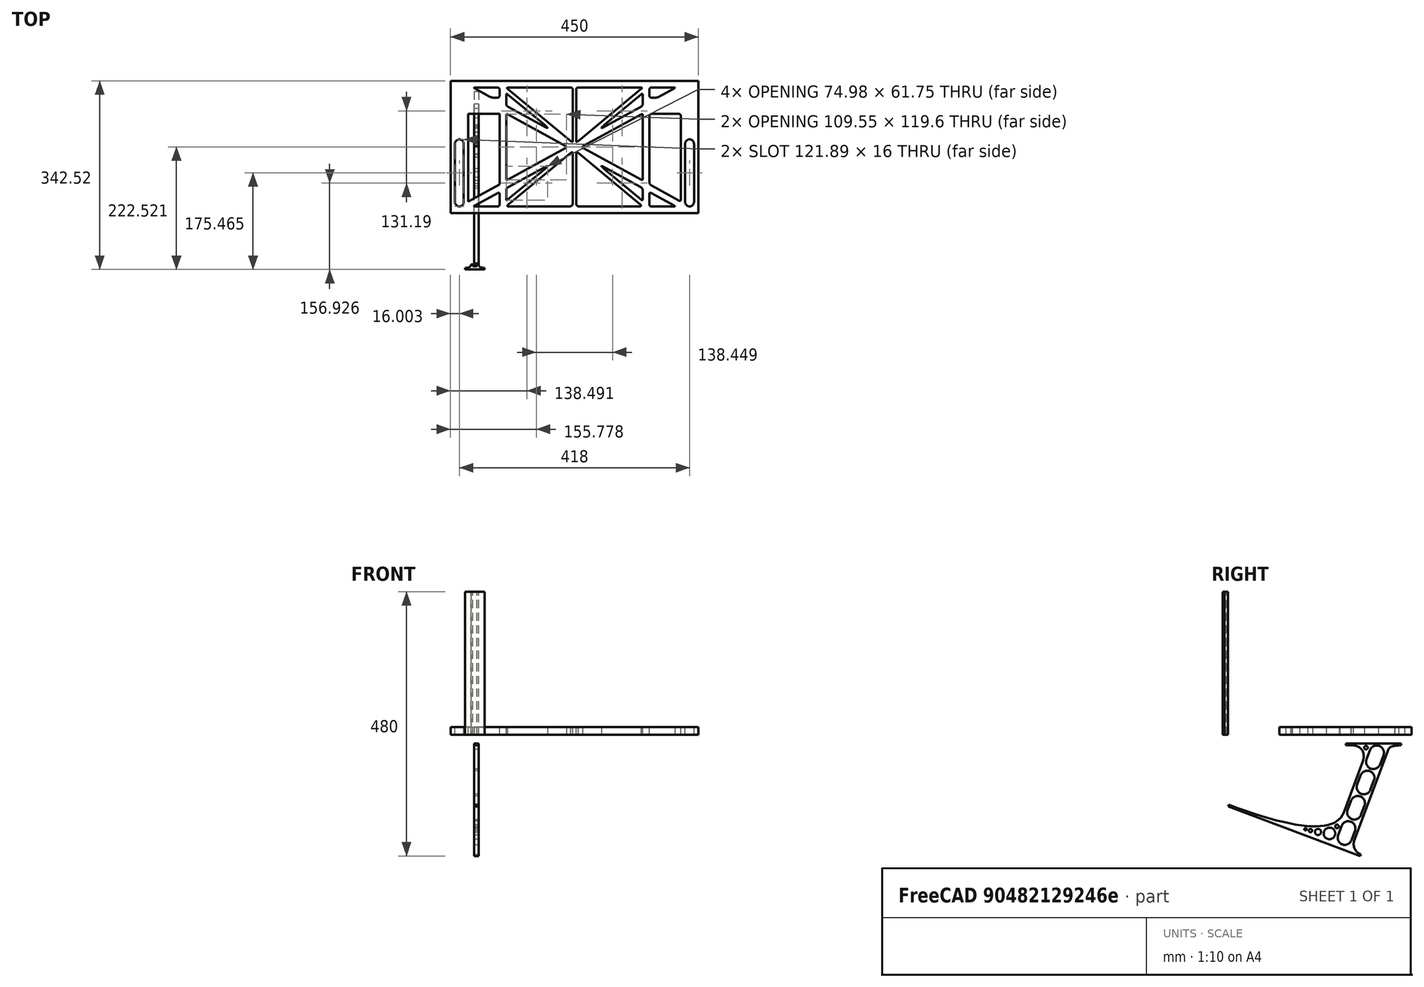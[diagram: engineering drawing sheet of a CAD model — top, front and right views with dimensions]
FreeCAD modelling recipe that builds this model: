
FCSTD DOCUMENT  (FreeCAD 0.19R0.19.2)
Label: laptopStand143FCStd
License: All rights reserved
LicenseURL: http://en.wikipedia.org/wiki/All_rights_reserved
objects: Sketcher::SketchObject×4, Part::Extrusion×3
note: 7 computed .brp shape members not serialized (recipe doc carries the construction recipe); baked Part::Feature solids carry a one-line shape summary decoded from their .brp

FEATURE [Sketcher::SketchObject] Sketch
  FullyConstrained = false
  sketch-geometry (349):
    g0: LineSegment StartX=-10.9272 StartY=-82.7794 StartZ=0 EndX=46.0728 EndY=-51.4823 EndZ=0
    g1: LineSegment StartX=-10.9272 StartY=76.4095 StartZ=0 EndX=-10.9272 EndY=-82.7794 EndZ=0
    g2: LineSegment StartX=46.0728 StartY=76.4095 StartZ=0 EndX=46.0728 EndY=-51.4823 EndZ=0
    g3: LineSegment StartX=-42.9272 StartY=136.221 StartZ=0 EndX=-42.9272 EndY=-103.779 EndZ=0
    g4: LineSegment StartX=407.073 StartY=136.221 StartZ=0 EndX=407.073 EndY=-103.779 EndZ=0
    g5: ArcOfCircle CenterX=-26.9272 CenterY=-83.7794 CenterZ=0 NormalX=0 NormalY=0 NormalZ=1 AngleXU=0 Radius=8 StartAngle=3.14159 EndAngle=6.28319
    g6: ArcOfCircle CenterX=391.073 CenterY=22.1087 CenterZ=0 NormalX=0 NormalY=0 NormalZ=1 AngleXU=0 Radius=8 StartAngle=-4.4e-15 EndAngle=3.14159
    g7: LineSegment StartX=399.073 StartY=22.1087 StartZ=0 EndX=399.073 EndY=-83.7794 EndZ=0
    g8: LineSegment StartX=383.073 StartY=22.1087 StartZ=0 EndX=383.073 EndY=-83.7794 EndZ=0
    g9: ArcOfCircle CenterX=391.073 CenterY=-83.7794 CenterZ=0 NormalX=0 NormalY=0 NormalZ=1 AngleXU=0 Radius=8 StartAngle=3.14159 EndAngle=6.28319
    g10: Circle CenterX=175.022 CenterY=27.0628 CenterZ=0 NormalX=0 NormalY=0 NormalZ=1 AngleXU=0 Radius=1
    g11: Circle CenterX=179.022 CenterY=24.8665 CenterZ=0 NormalX=0 NormalY=0 NormalZ=1 AngleXU=0 Radius=1
    g12: Circle CenterX=179.022 CenterY=27.0628 CenterZ=0 NormalX=0 NormalY=0 NormalZ=1 AngleXU=0 Radius=1
    g13: BSplineCurve PolesCount=3 KnotsCount=2 Degree=2 IsPeriodic=0
    g14: GeomPoint X=175.022 Y=27.0628 Z=0
    g15: GeomPoint X=179.022 Y=27.0628 Z=0
    g16: Circle CenterX=189.124 CenterY=27.0628 CenterZ=0 NormalX=0 NormalY=0 NormalZ=1 AngleXU=0 Radius=1
    g17: Circle CenterX=185.124 CenterY=24.8665 CenterZ=0 NormalX=0 NormalY=0 NormalZ=1 AngleXU=0 Radius=1
    g18: Circle CenterX=185.124 CenterY=27.0628 CenterZ=0 NormalX=0 NormalY=0 NormalZ=1 AngleXU=0 Radius=1
    g19: BSplineCurve PolesCount=3 KnotsCount=2 Degree=2 IsPeriodic=0
    g20: GeomPoint X=189.124 Y=27.0628 Z=0
    g21: GeomPoint X=185.124 Y=27.0628 Z=0
    g22: Circle CenterX=175.022 CenterY=5.37834 CenterZ=0 NormalX=0 NormalY=0 NormalZ=1 AngleXU=0 Radius=1
    g23: Circle CenterX=179.022 CenterY=7.57463 CenterZ=0 NormalX=0 NormalY=0 NormalZ=1 AngleXU=0 Radius=1
    g24: Circle CenterX=179.022 CenterY=5.34704 CenterZ=0 NormalX=0 NormalY=0 NormalZ=1 AngleXU=0 Radius=1
    g25: BSplineCurve PolesCount=3 KnotsCount=2 Degree=2 IsPeriodic=0
    g26: GeomPoint X=175.022 Y=5.37834 Z=0
    g27: GeomPoint X=179.022 Y=5.34704 Z=0
    g28: Circle CenterX=189.124 CenterY=5.37834 CenterZ=0 NormalX=0 NormalY=0 NormalZ=1 AngleXU=0 Radius=1
    g29: Circle CenterX=185.124 CenterY=7.57463 CenterZ=0 NormalX=0 NormalY=0 NormalZ=1 AngleXU=0 Radius=1
    g30: Circle CenterX=185.124 CenterY=5.34704 CenterZ=0 NormalX=0 NormalY=0 NormalZ=1 AngleXU=0 Radius=1
    g31: BSplineCurve PolesCount=3 KnotsCount=2 Degree=2 IsPeriodic=0
    g32: GeomPoint X=189.124 Y=5.37834 Z=0
    g33: GeomPoint X=185.124 Y=5.34704 Z=0
    g34: Circle CenterX=165.871 CenterY=18.1458 CenterZ=0 NormalX=0 NormalY=0 NormalZ=1 AngleXU=0 Radius=1
    g35: Circle CenterX=169.377 CenterY=16.2206 CenterZ=0 NormalX=0 NormalY=0 NormalZ=1 AngleXU=0 Radius=1
    g36: Circle CenterX=165.871 CenterY=14.2954 CenterZ=0 NormalX=0 NormalY=0 NormalZ=1 AngleXU=0 Radius=1
    g37: BSplineCurve PolesCount=3 KnotsCount=2 Degree=2 IsPeriodic=0
    g38: GeomPoint X=165.871 Y=18.1458 Z=0
    g39: GeomPoint X=165.871 Y=14.2954 Z=0
    g40: Circle CenterX=198.275 CenterY=18.1458 CenterZ=0 NormalX=0 NormalY=0 NormalZ=1 AngleXU=0 Radius=1
    g41: Circle CenterX=194.768 CenterY=16.2206 CenterZ=0 NormalX=0 NormalY=0 NormalZ=1 AngleXU=0 Radius=1
    g42: Circle CenterX=198.275 CenterY=14.2954 CenterZ=0 NormalX=0 NormalY=0 NormalZ=1 AngleXU=0 Radius=1
    g43: BSplineCurve PolesCount=3 KnotsCount=2 Degree=2 IsPeriodic=0
    g44: GeomPoint X=198.275 Y=18.1458 Z=0
    g45: GeomPoint X=198.275 Y=14.2954 Z=0
    g46: LineSegment StartX=407.073 StartY=-103.779 StartZ=0 EndX=-42.9272 EndY=-103.779 EndZ=0
    g47: LineSegment StartX=407.073 StartY=136.221 StartZ=0 EndX=-42.9272 EndY=136.221 EndZ=0
    g48: LineSegment StartX=46.0728 StartY=76.4095 StartZ=0 EndX=-10.9272 EndY=76.4095 EndZ=0
    g49: Circle CenterX=125.607 CenterY=54.1951 CenterZ=0 NormalX=0 NormalY=0 NormalZ=1 AngleXU=0 Radius=1
    g50: Circle CenterX=139.632 CenterY=46.4944 CenterZ=0 NormalX=0 NormalY=0 NormalZ=1 AngleXU=0 Radius=1
    g51: Circle CenterX=127.326 CenterY=56.7187 CenterZ=0 NormalX=0 NormalY=0 NormalZ=1 AngleXU=0 Radius=1
    g52: BSplineCurve PolesCount=3 KnotsCount=2 Degree=2 IsPeriodic=0
    g53: GeomPoint X=125.607 Y=54.1951 Z=0
    g54: GeomPoint X=127.326 Y=56.7187 Z=0
    g55: Circle CenterX=236.821 CenterY=56.7187 CenterZ=0 NormalX=0 NormalY=0 NormalZ=1 AngleXU=0 Radius=1
    g56: Circle CenterX=224.513 CenterY=46.4944 CenterZ=0 NormalX=0 NormalY=0 NormalZ=1 AngleXU=0 Radius=1
    g57: Circle CenterX=238.538 CenterY=54.1951 CenterZ=0 NormalX=0 NormalY=0 NormalZ=1 AngleXU=0 Radius=1
    g58: BSplineCurve PolesCount=3 KnotsCount=2 Degree=2 IsPeriodic=0
    g59: GeomPoint X=236.821 Y=56.7187 Z=0
    g60: GeomPoint X=238.538 Y=54.1951 Z=0
    g61: Circle CenterX=238.538 CenterY=-21.7539 CenterZ=0 NormalX=0 NormalY=0 NormalZ=1 AngleXU=0 Radius=1
    g62: Circle CenterX=224.513 CenterY=-14.0532 CenterZ=0 NormalX=0 NormalY=0 NormalZ=1 AngleXU=0 Radius=1
    g63: Circle CenterX=236.821 CenterY=-24.2775 CenterZ=0 NormalX=0 NormalY=0 NormalZ=1 AngleXU=0 Radius=1
    g64: BSplineCurve PolesCount=3 KnotsCount=2 Degree=2 IsPeriodic=0
    g65: GeomPoint X=238.538 Y=-21.7539 Z=0
    g66: GeomPoint X=236.821 Y=-24.2775 Z=0
    g67: Circle CenterX=125.607 CenterY=-21.7539 CenterZ=0 NormalX=0 NormalY=0 NormalZ=1 AngleXU=0 Radius=1
    g68: Circle CenterX=139.632 CenterY=-14.0532 CenterZ=0 NormalX=0 NormalY=0 NormalZ=1 AngleXU=0 Radius=1
    g69: Circle CenterX=127.325 CenterY=-24.2775 CenterZ=0 NormalX=0 NormalY=0 NormalZ=1 AngleXU=0 Radius=1
    g70: BSplineCurve PolesCount=3 KnotsCount=2 Degree=2 IsPeriodic=0
    g71: GeomPoint X=125.607 Y=-21.7539 Z=0
    g72: GeomPoint X=127.325 Y=-24.2775 Z=0
    g73: Circle CenterX=302.996 CenterY=111.695 CenterZ=0 NormalX=0 NormalY=0 NormalZ=1 AngleXU=0 Radius=1
    g74: Circle CenterX=306.073 CenterY=114.251 CenterZ=0 NormalX=0 NormalY=0 NormalZ=1 AngleXU=0 Radius=1
    g75: Circle CenterX=306.073 CenterY=110.251 CenterZ=0 NormalX=0 NormalY=0 NormalZ=1 AngleXU=0 Radius=1
    g76: BSplineCurve PolesCount=3 KnotsCount=2 Degree=2 IsPeriodic=0
    g77: GeomPoint X=302.996 Y=111.695 Z=0
    g78: GeomPoint X=306.073 Y=110.251 Z=0
    g79: Circle CenterX=306.073 CenterY=95.2763 CenterZ=0 NormalX=0 NormalY=0 NormalZ=1 AngleXU=0 Radius=1
    g80: Circle CenterX=306.073 CenterY=91.2763 CenterZ=0 NormalX=0 NormalY=0 NormalZ=1 AngleXU=0 Radius=1
    g81: Circle CenterX=302.567 CenterY=89.3511 CenterZ=0 NormalX=0 NormalY=0 NormalZ=1 AngleXU=0 Radius=1
    g82: BSplineCurve PolesCount=3 KnotsCount=2 Degree=2 IsPeriodic=0
    g83: GeomPoint X=306.073 Y=95.2763 Z=0
    g84: GeomPoint X=302.567 Y=89.3511 Z=0
    g85: LineSegment StartX=306.073 StartY=110.251 StartZ=0 EndX=306.073 EndY=95.2763 EndZ=0
    g86: LineSegment StartX=302.996 StartY=111.695 StartZ=0 EndX=236.821 EndY=56.7187 EndZ=0
    g87: LineSegment StartX=238.538 StartY=54.1951 StartZ=0 EndX=302.567 EndY=89.3511 EndZ=0
    g88: Circle CenterX=61.1496 CenterY=111.695 CenterZ=0 NormalX=0 NormalY=0 NormalZ=1 AngleXU=0 Radius=1
    g89: Circle CenterX=58.0728 CenterY=114.251 CenterZ=0 NormalX=0 NormalY=0 NormalZ=1 AngleXU=0 Radius=1
    g90: Circle CenterX=58.0728 CenterY=110.251 CenterZ=0 NormalX=0 NormalY=0 NormalZ=1 AngleXU=0 Radius=1
    g91: BSplineCurve PolesCount=3 KnotsCount=2 Degree=2 IsPeriodic=0
    g92: GeomPoint X=61.1496 Y=111.695 Z=0
    g93: GeomPoint X=58.0728 Y=110.251 Z=0
    g94: Circle CenterX=61.5791 CenterY=89.3511 CenterZ=0 NormalX=0 NormalY=0 NormalZ=1 AngleXU=0 Radius=1
    g95: Circle CenterX=58.0728 CenterY=91.2763 CenterZ=0 NormalX=0 NormalY=0 NormalZ=1 AngleXU=0 Radius=1
    g96: Circle CenterX=58.0728 CenterY=95.2763 CenterZ=0 NormalX=0 NormalY=0 NormalZ=1 AngleXU=0 Radius=1
    g97: BSplineCurve PolesCount=3 KnotsCount=2 Degree=2 IsPeriodic=0
    g98: GeomPoint X=61.5791 Y=89.3511 Z=0
    g99: GeomPoint X=58.0728 Y=95.2763 Z=0
    g100: LineSegment StartX=58.0728 StartY=110.251 StartZ=0 EndX=58.0728 EndY=95.2763 EndZ=0
    g101: LineSegment StartX=61.1496 StartY=111.695 StartZ=0 EndX=127.326 EndY=56.7187 EndZ=0
    g102: LineSegment StartX=125.607 StartY=54.1951 StartZ=0 EndX=61.5791 EndY=89.3511 EndZ=0
    g103: Circle CenterX=61.5791 CenterY=-56.9099 CenterZ=0 NormalX=0 NormalY=0 NormalZ=1 AngleXU=0 Radius=1
    g104: Circle CenterX=58.0728 CenterY=-58.8351 CenterZ=0 NormalX=0 NormalY=0 NormalZ=1 AngleXU=0 Radius=1
    g105: Circle CenterX=58.0728 CenterY=-62.8351 CenterZ=0 NormalX=0 NormalY=0 NormalZ=1 AngleXU=0 Radius=1
    g106: BSplineCurve PolesCount=3 KnotsCount=2 Degree=2 IsPeriodic=0
    g107: GeomPoint X=61.5791 Y=-56.9099 Z=0
    g108: GeomPoint X=58.0728 Y=-62.8351 Z=0
    g109: Circle CenterX=58.0728 CenterY=-77.8102 CenterZ=0 NormalX=0 NormalY=0 NormalZ=1 AngleXU=0 Radius=1
    g110: Circle CenterX=58.0728 CenterY=-81.8102 CenterZ=0 NormalX=0 NormalY=0 NormalZ=1 AngleXU=0 Radius=1
    g111: Circle CenterX=61.1496 CenterY=-79.2541 CenterZ=0 NormalX=0 NormalY=0 NormalZ=1 AngleXU=0 Radius=1
    g112: BSplineCurve PolesCount=3 KnotsCount=2 Degree=2 IsPeriodic=0
    g113: GeomPoint X=58.0728 Y=-77.8102 Z=0
    g114: GeomPoint X=61.1496 Y=-79.2541 Z=0
    g115: LineSegment StartX=58.0728 StartY=-62.8351 StartZ=0 EndX=58.0728 EndY=-77.8102 EndZ=0
    g116: LineSegment StartX=61.1496 StartY=-79.2541 StartZ=0 EndX=127.325 EndY=-24.2775 EndZ=0
    g117: LineSegment StartX=125.607 StartY=-21.7539 StartZ=0 EndX=61.5791 EndY=-56.9099 EndZ=0
    g118: Circle CenterX=302.567 CenterY=-56.9099 CenterZ=0 NormalX=0 NormalY=0 NormalZ=1 AngleXU=0 Radius=1
    g119: Circle CenterX=306.073 CenterY=-58.8351 CenterZ=0 NormalX=0 NormalY=0 NormalZ=1 AngleXU=0 Radius=1
    g120: Circle CenterX=306.073 CenterY=-62.8351 CenterZ=0 NormalX=0 NormalY=0 NormalZ=1 AngleXU=0 Radius=1
    g121: BSplineCurve PolesCount=3 KnotsCount=2 Degree=2 IsPeriodic=0
    g122: GeomPoint X=302.567 Y=-56.9099 Z=0
    g123: GeomPoint X=306.073 Y=-62.8351 Z=0
    g124: Circle CenterX=302.996 CenterY=-79.2541 CenterZ=0 NormalX=0 NormalY=0 NormalZ=1 AngleXU=0 Radius=1
    g125: Circle CenterX=306.073 CenterY=-81.8102 CenterZ=0 NormalX=0 NormalY=0 NormalZ=1 AngleXU=0 Radius=1
    g126: Circle CenterX=306.073 CenterY=-77.8102 CenterZ=0 NormalX=0 NormalY=0 NormalZ=1 AngleXU=0 Radius=1
    g127: BSplineCurve PolesCount=3 KnotsCount=2 Degree=2 IsPeriodic=0
    g128: GeomPoint X=302.996 Y=-79.2541 Z=0
    g129: GeomPoint X=306.073 Y=-77.8102 Z=0
    g130: LineSegment StartX=306.073 StartY=-62.8351 StartZ=0 EndX=306.073 EndY=-77.8102 EndZ=0
    g131: LineSegment StartX=302.996 StartY=-79.2541 StartZ=0 EndX=236.821 EndY=-24.2775 EndZ=0
    g132: LineSegment StartX=238.538 StartY=-21.7539 StartZ=0 EndX=302.567 EndY=-56.9099 EndZ=0
    g133: Circle CenterX=61.6457 CenterY=-88.8112 CenterZ=0 NormalX=0 NormalY=0 NormalZ=1 AngleXU=0 Radius=1
    g134: Circle CenterX=58.0728 CenterY=-91.7794 CenterZ=0 NormalX=0 NormalY=0 NormalZ=1 AngleXU=0 Radius=1
    g135: Circle CenterX=63.9135 CenterY=-91.7794 CenterZ=0 NormalX=0 NormalY=0 NormalZ=1 AngleXU=0 Radius=1
    g136: BSplineCurve PolesCount=3 KnotsCount=2 Degree=2 IsPeriodic=0
    g137: GeomPoint X=61.6457 Y=-88.8112 Z=0
    g138: GeomPoint X=63.9135 Y=-91.7794 Z=0
    g139: Circle CenterX=179.022 CenterY=-85.8163 CenterZ=0 NormalX=0 NormalY=0 NormalZ=1 AngleXU=0 Radius=1
    g140: Circle CenterX=179.022 CenterY=-91.7794 CenterZ=0 NormalX=0 NormalY=0 NormalZ=1 AngleXU=0 Radius=1
    g141: Circle CenterX=171.895 CenterY=-91.7794 CenterZ=0 NormalX=0 NormalY=0 NormalZ=1 AngleXU=0 Radius=1
    g142: BSplineCurve PolesCount=3 KnotsCount=2 Degree=2 IsPeriodic=0
    g143: GeomPoint X=179.022 Y=-85.8163 Z=0
    g144: GeomPoint X=171.895 Y=-91.7794 Z=0
    g145: Circle CenterX=185.124 CenterY=-86.2028 CenterZ=0 NormalX=0 NormalY=0 NormalZ=1 AngleXU=0 Radius=1
    g146: Circle CenterX=185.124 CenterY=-91.7794 CenterZ=0 NormalX=0 NormalY=0 NormalZ=1 AngleXU=0 Radius=1
    g147: Circle CenterX=191.747 CenterY=-91.7794 CenterZ=0 NormalX=0 NormalY=0 NormalZ=1 AngleXU=0 Radius=1
    g148: BSplineCurve PolesCount=3 KnotsCount=2 Degree=2 IsPeriodic=0
    g149: GeomPoint X=185.124 Y=-86.2028 Z=0
    g150: GeomPoint X=191.747 Y=-91.7794 Z=0
    g151: Circle CenterX=299.888 CenterY=-86.6413 CenterZ=0 NormalX=0 NormalY=0 NormalZ=1 AngleXU=0 Radius=1
    g152: Circle CenterX=306.073 CenterY=-91.7794 CenterZ=0 NormalX=0 NormalY=0 NormalZ=1 AngleXU=0 Radius=1
    g153: Circle CenterX=298.776 CenterY=-91.7794 CenterZ=0 NormalX=0 NormalY=0 NormalZ=1 AngleXU=0 Radius=1
    g154: BSplineCurve PolesCount=3 KnotsCount=2 Degree=2 IsPeriodic=0
    g155: GeomPoint X=299.888 Y=-86.6413 Z=0
    g156: GeomPoint X=298.776 Y=-91.7794 Z=0
    g157: LineSegment StartX=189.124 StartY=5.37834 StartZ=0 EndX=299.888 EndY=-86.6413 EndZ=0
    g158: LineSegment StartX=298.776 StartY=-91.7794 StartZ=0 EndX=191.747 EndY=-91.7794 EndZ=0
    g159: LineSegment StartX=185.124 StartY=-86.2028 StartZ=0 EndX=185.124 EndY=5.34704 EndZ=0
    g160: LineSegment StartX=179.022 StartY=5.34704 StartZ=0 EndX=179.022 EndY=-85.8163 EndZ=0
    g161: LineSegment StartX=171.895 StartY=-91.7794 StartZ=0 EndX=63.9135 EndY=-91.7794 EndZ=0
    g162: LineSegment StartX=61.6457 StartY=-88.8112 StartZ=0 EndX=175.022 EndY=5.37834 EndZ=0
    g163: Circle CenterX=302.073 CenterY=124.221 CenterZ=0 NormalX=0 NormalY=0 NormalZ=1 AngleXU=0 Radius=1
    g164: Circle CenterX=306.073 CenterY=124.221 CenterZ=0 NormalX=0 NormalY=0 NormalZ=1 AngleXU=0 Radius=1
    g165: Circle CenterX=302.996 CenterY=121.665 CenterZ=0 NormalX=0 NormalY=0 NormalZ=1 AngleXU=0 Radius=1
    g166: BSplineCurve PolesCount=3 KnotsCount=2 Degree=2 IsPeriodic=0
    g167: GeomPoint X=302.073 Y=124.221 Z=0
    g168: GeomPoint X=302.996 Y=121.665 Z=0
    g169: Circle CenterX=189.124 CenterY=124.221 CenterZ=0 NormalX=0 NormalY=0 NormalZ=1 AngleXU=0 Radius=1
    g170: Circle CenterX=185.124 CenterY=124.221 CenterZ=0 NormalX=0 NormalY=0 NormalZ=1 AngleXU=0 Radius=1
    g171: Circle CenterX=185.124 CenterY=120.221 CenterZ=0 NormalX=0 NormalY=0 NormalZ=1 AngleXU=0 Radius=1
    g172: BSplineCurve PolesCount=3 KnotsCount=2 Degree=2 IsPeriodic=0
    g173: GeomPoint X=189.124 Y=124.221 Z=0
    g174: GeomPoint X=185.124 Y=120.221 Z=0
    g175: Circle CenterX=175.022 CenterY=124.221 CenterZ=0 NormalX=0 NormalY=0 NormalZ=1 AngleXU=0 Radius=1
    g176: Circle CenterX=179.022 CenterY=124.221 CenterZ=0 NormalX=0 NormalY=0 NormalZ=1 AngleXU=0 Radius=1
    g177: Circle CenterX=179.022 CenterY=120.221 CenterZ=0 NormalX=0 NormalY=0 NormalZ=1 AngleXU=0 Radius=1
    g178: BSplineCurve PolesCount=3 KnotsCount=2 Degree=2 IsPeriodic=0
    g179: GeomPoint X=175.022 Y=124.221 Z=0
    g180: GeomPoint X=179.022 Y=120.221 Z=0
    g181: Circle CenterX=62.0728 CenterY=124.221 CenterZ=0 NormalX=0 NormalY=0 NormalZ=1 AngleXU=0 Radius=1
    g182: Circle CenterX=58.0728 CenterY=124.221 CenterZ=0 NormalX=0 NormalY=0 NormalZ=1 AngleXU=0 Radius=1
    g183: Circle CenterX=61.1496 CenterY=121.665 CenterZ=0 NormalX=0 NormalY=0 NormalZ=1 AngleXU=0 Radius=1
    g184: BSplineCurve PolesCount=3 KnotsCount=2 Degree=2 IsPeriodic=0
    g185: GeomPoint X=62.0728 Y=124.221 Z=0
    g186: GeomPoint X=61.1496 Y=121.665 Z=0
    g187: LineSegment StartX=62.0728 StartY=124.221 StartZ=0 EndX=175.022 EndY=124.221 EndZ=0
    g188: LineSegment StartX=179.022 StartY=120.221 StartZ=0 EndX=179.022 EndY=27.0628 EndZ=0
    g189: LineSegment StartX=185.124 StartY=27.0628 StartZ=0 EndX=185.124 EndY=120.221 EndZ=0
    g190: LineSegment StartX=189.124 StartY=124.221 StartZ=0 EndX=302.073 EndY=124.221 EndZ=0
    g191: LineSegment StartX=302.996 StartY=121.665 StartZ=0 EndX=189.124 EndY=27.0628 EndZ=0
    g192: LineSegment StartX=175.022 StartY=27.0628 StartZ=0 EndX=61.1496 EndY=121.665 EndZ=0
    g193: Circle CenterX=61.5791 CenterY=75.4095 CenterZ=0 NormalX=0 NormalY=0 NormalZ=1 AngleXU=0 Radius=1
    g194: Circle CenterX=58.0728 CenterY=77.3346 CenterZ=0 NormalX=0 NormalY=0 NormalZ=1 AngleXU=0 Radius=1
    g195: Circle CenterX=58.0728 CenterY=73.3346 CenterZ=0 NormalX=0 NormalY=0 NormalZ=1 AngleXU=0 Radius=1
    g196: BSplineCurve PolesCount=3 KnotsCount=2 Degree=2 IsPeriodic=0
    g197: GeomPoint X=61.5791 Y=75.4095 Z=0
    g198: GeomPoint X=58.0728 Y=73.3346 Z=0
    g199: Circle CenterX=58.0728 CenterY=-40.8935 CenterZ=0 NormalX=0 NormalY=0 NormalZ=1 AngleXU=0 Radius=1
    g200: Circle CenterX=58.0728 CenterY=-44.8935 CenterZ=0 NormalX=0 NormalY=0 NormalZ=1 AngleXU=0 Radius=1
    g201: Circle CenterX=61.5791 CenterY=-42.9683 CenterZ=0 NormalX=0 NormalY=0 NormalZ=1 AngleXU=0 Radius=1
    g202: BSplineCurve PolesCount=3 KnotsCount=2 Degree=2 IsPeriodic=0
    g203: GeomPoint X=58.0728 Y=-40.8935 Z=0
    g204: GeomPoint X=61.5791 Y=-42.9683 Z=0
    g205: LineSegment StartX=61.5791 StartY=-42.9683 StartZ=0 EndX=165.871 EndY=14.2954 EndZ=0
    g206: LineSegment StartX=165.871 StartY=18.1458 StartZ=0 EndX=61.5791 EndY=75.4095 EndZ=0
    g207: LineSegment StartX=58.0728 StartY=73.3346 StartZ=0 EndX=58.0728 EndY=-40.8935 EndZ=0
    g208: Circle CenterX=302.567 CenterY=-42.9683 CenterZ=0 NormalX=0 NormalY=0 NormalZ=1 AngleXU=0 Radius=1
    g209: Circle CenterX=306.073 CenterY=-44.8935 CenterZ=0 NormalX=0 NormalY=0 NormalZ=1 AngleXU=0 Radius=1
    g210: Circle CenterX=306.073 CenterY=-40.8935 CenterZ=0 NormalX=0 NormalY=0 NormalZ=1 AngleXU=0 Radius=1
    g211: BSplineCurve PolesCount=3 KnotsCount=2 Degree=2 IsPeriodic=0
    g212: GeomPoint X=302.567 Y=-42.9683 Z=0
    g213: GeomPoint X=306.073 Y=-40.8935 Z=0
    g214: Circle CenterX=306.073 CenterY=73.3346 CenterZ=0 NormalX=0 NormalY=0 NormalZ=1 AngleXU=0 Radius=1
    g215: Circle CenterX=306.073 CenterY=77.3346 CenterZ=0 NormalX=0 NormalY=0 NormalZ=1 AngleXU=0 Radius=1
    g216: Circle CenterX=302.567 CenterY=75.4095 CenterZ=0 NormalX=0 NormalY=0 NormalZ=1 AngleXU=0 Radius=1
    g217: BSplineCurve PolesCount=3 KnotsCount=2 Degree=2 IsPeriodic=0
    g218: GeomPoint X=306.073 Y=73.3346 Z=0
    g219: GeomPoint X=302.567 Y=75.4095 Z=0
    g220: LineSegment StartX=302.567 StartY=-42.9683 StartZ=0 EndX=198.275 EndY=14.2954 EndZ=0
    g221: LineSegment StartX=198.275 StartY=18.1458 StartZ=0 EndX=302.567 EndY=75.4095 EndZ=0
    g222: LineSegment StartX=306.073 StartY=73.3346 StartZ=0 EndX=306.073 EndY=-40.8935 EndZ=0
    g223: LineSegment StartX=322.073 StartY=105.865 StartZ=0 EndX=328.643 EndY=105.865 EndZ=0
    g224: LineSegment StartX=318.073 StartY=120.221 StartZ=0 EndX=318.073 EndY=109.865 EndZ=0
    g225: LineSegment StartX=336.157 StartY=107.779 StartZ=0 EndX=362.567 EndY=122.294 EndZ=0
    g226: Circle CenterX=362.073 CenterY=124.221 CenterZ=0 NormalX=0 NormalY=0 NormalZ=1 AngleXU=0 Radius=1
    g227: Circle CenterX=366.073 CenterY=124.221 CenterZ=0 NormalX=0 NormalY=0 NormalZ=1 AngleXU=0 Radius=1
    g228: Circle CenterX=362.567 CenterY=122.294 CenterZ=0 NormalX=0 NormalY=0 NormalZ=1 AngleXU=0 Radius=1
    g229: BSplineCurve PolesCount=3 KnotsCount=2 Degree=2 IsPeriodic=0
    g230: GeomPoint X=362.073 Y=124.221 Z=0
    g231: GeomPoint X=362.567 Y=122.294 Z=0
    g232: Circle CenterX=322.073 CenterY=124.221 CenterZ=0 NormalX=0 NormalY=0 NormalZ=1 AngleXU=0 Radius=1
    g233: Circle CenterX=318.073 CenterY=124.221 CenterZ=0 NormalX=0 NormalY=0 NormalZ=1 AngleXU=0 Radius=1
    g234: Circle CenterX=318.073 CenterY=120.221 CenterZ=0 NormalX=0 NormalY=0 NormalZ=1 AngleXU=0 Radius=1
    g235: BSplineCurve PolesCount=3 KnotsCount=2 Degree=2 IsPeriodic=0
    g236: GeomPoint X=322.073 Y=124.221 Z=0
    g237: GeomPoint X=318.073 Y=120.221 Z=0
    g238: Circle CenterX=322.073 CenterY=105.865 CenterZ=0 NormalX=0 NormalY=0 NormalZ=1 AngleXU=0 Radius=1
    g239: Circle CenterX=318.073 CenterY=105.865 CenterZ=0 NormalX=0 NormalY=0 NormalZ=1 AngleXU=0 Radius=1
    g240: Circle CenterX=318.073 CenterY=109.865 CenterZ=0 NormalX=0 NormalY=0 NormalZ=1 AngleXU=0 Radius=1
    g241: BSplineCurve PolesCount=3 KnotsCount=2 Degree=2 IsPeriodic=0
    g242: GeomPoint X=322.073 Y=105.865 Z=0
    g243: GeomPoint X=318.073 Y=109.865 Z=0
    g244: Circle CenterX=336.157 CenterY=107.779 CenterZ=0 NormalX=0 NormalY=0 NormalZ=1 AngleXU=0 Radius=1
    g245: Circle CenterX=332.651 CenterY=105.853 CenterZ=0 NormalX=0 NormalY=0 NormalZ=1 AngleXU=0 Radius=1
    g246: Circle CenterX=328.643 CenterY=105.865 CenterZ=0 NormalX=0 NormalY=0 NormalZ=1 AngleXU=0 Radius=1
    g247: BSplineCurve PolesCount=3 KnotsCount=2 Degree=2 IsPeriodic=0
    g248: GeomPoint X=336.157 Y=107.779 Z=0
    g249: GeomPoint X=328.643 Y=105.865 Z=0
    g250: LineSegment StartX=322.073 StartY=124.221 StartZ=0 EndX=362.073 EndY=124.221 EndZ=0
    g251: Circle CenterX=371.567 CenterY=-80.8644 CenterZ=0 NormalX=0 NormalY=0 NormalZ=1 AngleXU=0 Radius=1
    g252: Circle CenterX=375.073 CenterY=-82.7896 CenterZ=0 NormalX=0 NormalY=0 NormalZ=1 AngleXU=0 Radius=1
    g253: Circle CenterX=375.073 CenterY=-78.7896 CenterZ=0 NormalX=0 NormalY=0 NormalZ=1 AngleXU=0 Radius=1
    g254: BSplineCurve PolesCount=3 KnotsCount=2 Degree=2 IsPeriodic=0
    g255: GeomPoint X=371.567 Y=-80.8644 Z=0
    g256: GeomPoint X=375.073 Y=-78.7896 Z=0
    g257: Circle CenterX=321.579 CenterY=-53.4075 CenterZ=0 NormalX=0 NormalY=0 NormalZ=1 AngleXU=0 Radius=1
    g258: Circle CenterX=318.073 CenterY=-51.4823 CenterZ=0 NormalX=0 NormalY=0 NormalZ=1 AngleXU=0 Radius=1
    g259: Circle CenterX=318.073 CenterY=-47.4805 CenterZ=0 NormalX=0 NormalY=0 NormalZ=1 AngleXU=0 Radius=1
    g260: BSplineCurve PolesCount=3 KnotsCount=2 Degree=2 IsPeriodic=0
    g261: GeomPoint X=321.579 Y=-53.4075 Z=0
    g262: GeomPoint X=318.073 Y=-47.4805 Z=0
    g263: LineSegment StartX=371.567 StartY=-80.8644 StartZ=0 EndX=321.579 EndY=-53.4075 EndZ=0
    g264: Circle CenterX=321.579 CenterY=-67.3492 CenterZ=0 NormalX=0 NormalY=0 NormalZ=1 AngleXU=0 Radius=1
    g265: Circle CenterX=318.073 CenterY=-65.424 CenterZ=0 NormalX=0 NormalY=0 NormalZ=1 AngleXU=0 Radius=1
    g266: Circle CenterX=318.073 CenterY=-69.424 CenterZ=0 NormalX=0 NormalY=0 NormalZ=1 AngleXU=0 Radius=1
    g267: BSplineCurve PolesCount=3 KnotsCount=2 Degree=2 IsPeriodic=0
    g268: GeomPoint X=321.579 Y=-67.3492 Z=0
    g269: GeomPoint X=318.073 Y=-69.424 Z=0
    g270: Circle CenterX=362.567 CenterY=-89.8542 CenterZ=0 NormalX=0 NormalY=0 NormalZ=1 AngleXU=0 Radius=1
    g271: Circle CenterX=366.073 CenterY=-91.7794 CenterZ=0 NormalX=0 NormalY=0 NormalZ=1 AngleXU=0 Radius=1
    g272: Circle CenterX=362.073 CenterY=-91.7794 CenterZ=0 NormalX=0 NormalY=0 NormalZ=1 AngleXU=0 Radius=1
    g273: BSplineCurve PolesCount=3 KnotsCount=2 Degree=2 IsPeriodic=0
    g274: GeomPoint X=362.567 Y=-89.8542 Z=0
    g275: GeomPoint X=362.073 Y=-91.7794 Z=0
    g276: Circle CenterX=322.073 CenterY=-91.7794 CenterZ=0 NormalX=0 NormalY=0 NormalZ=1 AngleXU=0 Radius=1
    g277: Circle CenterX=318.073 CenterY=-91.7794 CenterZ=0 NormalX=0 NormalY=0 NormalZ=1 AngleXU=0 Radius=1
    g278: Circle CenterX=318.073 CenterY=-87.7794 CenterZ=0 NormalX=0 NormalY=0 NormalZ=1 AngleXU=0 Radius=1
    g279: BSplineCurve PolesCount=3 KnotsCount=2 Degree=2 IsPeriodic=0
    g280: GeomPoint X=322.073 Y=-91.7794 Z=0
    g281: GeomPoint X=318.073 Y=-87.7794 Z=0
    g282: LineSegment StartX=362.567 StartY=-89.8542 StartZ=0 EndX=321.579 EndY=-67.3492 EndZ=0
    g283: LineSegment StartX=318.073 StartY=-69.424 StartZ=0 EndX=318.073 EndY=-87.7794 EndZ=0
    g284: LineSegment StartX=322.073 StartY=-91.7794 StartZ=0 EndX=362.073 EndY=-91.7794 EndZ=0
    g285: Circle CenterX=2.07281 CenterY=124.221 CenterZ=0 NormalX=0 NormalY=0 NormalZ=1 AngleXU=0 Radius=1
    g286: Circle CenterX=1.57905 CenterY=122.295 CenterZ=0 NormalX=0 NormalY=0 NormalZ=1 AngleXU=0 Radius=1
    g287: BSplineCurve PolesCount=3 KnotsCount=2 Degree=2 IsPeriodic=0
    g288: GeomPoint X=2.07281 Y=124.221 Z=0
    g289: GeomPoint X=1.57905 Y=122.295 Z=0
    g290: Circle CenterX=42.0728 CenterY=124.221 CenterZ=0 NormalX=0 NormalY=0 NormalZ=1 AngleXU=0 Radius=1
    g291: Circle CenterX=46.0728 CenterY=124.221 CenterZ=0 NormalX=0 NormalY=0 NormalZ=1 AngleXU=0 Radius=1
    g292: Circle CenterX=46.0728 CenterY=120.221 CenterZ=0 NormalX=0 NormalY=0 NormalZ=1 AngleXU=0 Radius=1
    g293: BSplineCurve PolesCount=3 KnotsCount=2 Degree=2 IsPeriodic=0
    g294: GeomPoint X=42.0728 Y=124.221 Z=0
    g295: GeomPoint X=46.0728 Y=120.221 Z=0
    g296: Circle CenterX=46.0728 CenterY=109.865 CenterZ=0 NormalX=0 NormalY=0 NormalZ=1 AngleXU=0 Radius=1
    g297: Circle CenterX=46.0728 CenterY=105.865 CenterZ=0 NormalX=0 NormalY=0 NormalZ=1 AngleXU=0 Radius=1
    g298: Circle CenterX=42.0728 CenterY=105.865 CenterZ=0 NormalX=0 NormalY=0 NormalZ=1 AngleXU=0 Radius=1
    g299: BSplineCurve PolesCount=3 KnotsCount=2 Degree=2 IsPeriodic=0
    g300: GeomPoint X=46.0728 Y=109.865 Z=0
    g301: GeomPoint X=42.0728 Y=105.865 Z=0
    g302: Circle CenterX=35.5028 CenterY=105.865 CenterZ=0 NormalX=0 NormalY=0 NormalZ=1 AngleXU=0 Radius=1
    g303: Circle CenterX=31.5028 CenterY=105.865 CenterZ=0 NormalX=0 NormalY=0 NormalZ=1 AngleXU=0 Radius=1
    g304: Circle CenterX=27.9965 CenterY=107.79 CenterZ=0 NormalX=0 NormalY=0 NormalZ=1 AngleXU=0 Radius=1
    g305: BSplineCurve PolesCount=3 KnotsCount=2 Degree=2 IsPeriodic=0
    g306: GeomPoint X=35.5028 Y=105.865 Z=0
    g307: GeomPoint X=27.9965 Y=107.79 Z=0
    g308: LineSegment StartX=2.07281 StartY=124.221 StartZ=0 EndX=42.0728 EndY=124.221 EndZ=0
    g309: LineSegment StartX=46.0728 StartY=120.221 StartZ=0 EndX=46.0728 EndY=109.865 EndZ=0
    g310: LineSegment StartX=42.0728 StartY=105.865 StartZ=0 EndX=35.5028 EndY=105.865 EndZ=0
    g311: LineSegment StartX=27.9965 StartY=107.79 StartZ=0 EndX=1.57905 EndY=122.295 EndZ=0
    g312: Circle CenterX=42.5666 CenterY=-67.3492 CenterZ=0 NormalX=0 NormalY=0 NormalZ=1 AngleXU=0 Radius=1
    g313: Circle CenterX=46.0728 CenterY=-65.424 CenterZ=0 NormalX=0 NormalY=0 NormalZ=1 AngleXU=0 Radius=1
    g314: Circle CenterX=46.0728 CenterY=-69.424 CenterZ=0 NormalX=0 NormalY=0 NormalZ=1 AngleXU=0 Radius=1
    g315: BSplineCurve PolesCount=3 KnotsCount=2 Degree=2 IsPeriodic=0
    g316: GeomPoint X=42.5666 Y=-67.3492 Z=0
    g317: GeomPoint X=46.0728 Y=-69.424 Z=0
    g318: Circle CenterX=46.0728 CenterY=-87.7794 CenterZ=0 NormalX=0 NormalY=0 NormalZ=1 AngleXU=0 Radius=1
    g319: Circle CenterX=46.0728 CenterY=-91.7794 CenterZ=0 NormalX=0 NormalY=0 NormalZ=1 AngleXU=0 Radius=1
    g320: Circle CenterX=42.0728 CenterY=-91.7794 CenterZ=0 NormalX=0 NormalY=0 NormalZ=1 AngleXU=0 Radius=1
    g321: BSplineCurve PolesCount=3 KnotsCount=2 Degree=2 IsPeriodic=0
    g322: GeomPoint X=46.0728 Y=-87.7794 Z=0
    g323: GeomPoint X=42.0728 Y=-91.7794 Z=0
    g324: Circle CenterX=2.07281 CenterY=-91.7794 CenterZ=0 NormalX=0 NormalY=0 NormalZ=1 AngleXU=0 Radius=1
    g325: Circle CenterX=-1.92719 CenterY=-91.7794 CenterZ=0 NormalX=0 NormalY=0 NormalZ=1 AngleXU=0 Radius=1
    g326: Circle CenterX=1.57905 CenterY=-89.8542 CenterZ=0 NormalX=0 NormalY=0 NormalZ=1 AngleXU=0 Radius=1
    g327: BSplineCurve PolesCount=3 KnotsCount=2 Degree=2 IsPeriodic=0
    g328: GeomPoint X=2.07281 Y=-91.7794 Z=0
    g329: GeomPoint X=1.57905 Y=-89.8542 Z=0
    g330: LineSegment StartX=2.07281 StartY=-91.7794 StartZ=0 EndX=42.0728 EndY=-91.7794 EndZ=0
    g331: LineSegment StartX=46.0728 StartY=-87.7794 StartZ=0 EndX=46.0728 EndY=-69.424 EndZ=0
    g332: LineSegment StartX=42.5666 StartY=-67.3492 StartZ=0 EndX=1.57905 EndY=-89.8542 EndZ=0
    g333: Circle CenterX=322.073 CenterY=76.4095 CenterZ=0 NormalX=0 NormalY=0 NormalZ=1 AngleXU=0 Radius=4
    g334: BSplineCurve PolesCount=3 KnotsCount=2 Degree=2 IsPeriodic=0
    g335: GeomPoint X=318.073 Y=72.4095 Z=0
    g336: GeomPoint X=322.073 Y=76.4095 Z=0
    g337: Circle CenterX=375.073 CenterY=72.4095 CenterZ=0 NormalX=0 NormalY=0 NormalZ=1 AngleXU=0 Radius=1
    g338: Circle CenterX=375.073 CenterY=76.4095 CenterZ=0 NormalX=0 NormalY=0 NormalZ=1 AngleXU=0 Radius=1
    g339: Circle CenterX=371.073 CenterY=76.4095 CenterZ=0 NormalX=0 NormalY=0 NormalZ=1 AngleXU=0 Radius=1
    g340: BSplineCurve PolesCount=3 KnotsCount=2 Degree=2 IsPeriodic=0
    g341: GeomPoint X=375.073 Y=72.4095 Z=0
    g342: GeomPoint X=371.073 Y=76.4095 Z=0
    g343: LineSegment StartX=322.073 StartY=76.4095 StartZ=0 EndX=371.073 EndY=76.4095 EndZ=0
    g344: LineSegment StartX=318.073 StartY=72.4095 StartZ=0 EndX=318.073 EndY=-47.4805 EndZ=0
    g345: LineSegment StartX=375.073 StartY=72.4095 StartZ=0 EndX=375.073 EndY=-78.7896 EndZ=0
    g346: ArcOfCircle CenterX=-26.9272 CenterY=22.1087 CenterZ=0 NormalX=0 NormalY=0 NormalZ=1 AngleXU=0 Radius=4 StartAngle=5e-16 EndAngle=3.14159
    g347: LineSegment StartX=-30.9272 StartY=22.1087 StartZ=0 EndX=-34.9272 EndY=-83.7794 EndZ=0
    g348: LineSegment StartX=-18.9272 StartY=-83.7794 StartZ=0 EndX=-22.9272 EndY=22.1087 EndZ=0
  constraints (572):
    c: Coincident(g0,g2)
    c: Block(g0)
    c: Block(g1)
    c: Vertical(g3)
    c: Vertical(g4)
    c: Block(g4)
    c: Block(g3)
    c: Tangent(g6,g7) = 1.5708
    c: Tangent(g7,g9) = 1.5708
    c: Equal(g6,g9)
    c: Coincident(g8,g6)
    c: Coincident(g8,g9)
    c: Block(g7)
    c: Block(g8)
    c: Weight(g10) = 1
    c: Equal(g10,g11)
    c: Equal(g10,g12)
    c: InternalAlignment(g10,g13)
    c: InternalAlignment(g11,g13)
    c: InternalAlignment(g12,g13)
    c: InternalAlignment(g14,g13)
    c: InternalAlignment(g15,g13)
    c: Weight(g16) = 1
    c: Equal(g16,g17)
    c: Equal(g16,g18)
    c: InternalAlignment(g16,g19)
    c: InternalAlignment(g17,g19)
    c: InternalAlignment(g18,g19)
    c: InternalAlignment(g20,g19)
    c: InternalAlignment(g21,g19)
    c: Block(g19)
    c: Block(g13)
    c: Weight(g22) = 1
    c: Equal(g22,g23)
    c: Equal(g22,g24)
    c: InternalAlignment(g22,g25)
    c: InternalAlignment(g23,g25)
    c: InternalAlignment(g24,g25)
    c: InternalAlignment(g26,g25)
    c: InternalAlignment(g27,g25)
    c: Weight(g28) = 1
    c: Equal(g28,g29)
    c: Equal(g28,g30)
    c: InternalAlignment(g28,g31)
    c: InternalAlignment(g29,g31)
    c: InternalAlignment(g30,g31)
    c: InternalAlignment(g32,g31)
    c: InternalAlignment(g33,g31)
    c: Block(g31)
    c: Block(g25)
    c: Weight(g34) = 1
    c: Equal(g34,g35)
    c: Equal(g34,g36)
    c: InternalAlignment(g34,g37)
    c: InternalAlignment(g35,g37)
    c: InternalAlignment(g36,g37)
    c: InternalAlignment(g38,g37)
    c: InternalAlignment(g39,g37)
    c: Weight(g40) = 1
    c: Equal(g40,g41)
    c: Equal(g40,g42)
    c: InternalAlignment(g40,g43)
    c: InternalAlignment(g41,g43)
    c: InternalAlignment(g42,g43)
    c: InternalAlignment(g44,g43)
    c: InternalAlignment(g45,g43)
    c: Block(g37)
    c: Block(g43)
    c: Coincident(g46,g4)
    c: Coincident(g46,g3)
    c: Horizontal(g46)
    c: Distance(g46) = 450
    c: Coincident(g47,g4)
    c: Coincident(g47,g3)
    c: Horizontal(g47)
    c: Horizontal(g48)
    c: Coincident(g2,g48)
    c: Block(g48)
    c: Coincident(g1,g48)
    c: Weight(g49) = 1
    c: Equal(g49,g50)
    c: Equal(g49,g51)
    c: InternalAlignment(g49,g52)
    c: InternalAlignment(g50,g52)
    c: InternalAlignment(g51,g52)
    c: InternalAlignment(g53,g52)
    c: InternalAlignment(g54,g52)
    c: Block(g52)
    c: Weight(g55) = 1
    c: Equal(g55,g56)
    c: Equal(g55,g57)
    c: InternalAlignment(g55,g58)
    c: InternalAlignment(g56,g58)
    c: InternalAlignment(g57,g58)
    c: InternalAlignment(g59,g58)
    c: InternalAlignment(g60,g58)
    c: Block(g58)
    c: Weight(g61) = 1
    c: Equal(g61,g62)
    c: Equal(g61,g63)
    c: InternalAlignment(g61,g64)
    c: InternalAlignment(g62,g64)
    c: InternalAlignment(g63,g64)
    c: InternalAlignment(g65,g64)
    c: InternalAlignment(g66,g64)
    c: Block(g64)
    c: Weight(g67) = 1
    c: Equal(g67,g68)
    c: Equal(g67,g69)
    c: InternalAlignment(g67,g70)
    c: InternalAlignment(g68,g70)
    c: InternalAlignment(g69,g70)
    c: InternalAlignment(g71,g70)
    c: InternalAlignment(g72,g70)
    c: Block(g70)
    c: Weight(g73) = 1
    c: Equal(g73,g74)
    c: Equal(g73,g75)
    c: InternalAlignment(g73,g76)
    c: InternalAlignment(g74,g76)
    c: InternalAlignment(g75,g76)
    c: InternalAlignment(g77,g76)
    c: InternalAlignment(g78,g76)
    c: Weight(g79) = 1
    c: Equal(g79,g80)
    c: Equal(g79,g81)
    c: InternalAlignment(g79,g82)
    c: InternalAlignment(g80,g82)
    c: InternalAlignment(g81,g82)
    c: InternalAlignment(g83,g82)
    c: InternalAlignment(g84,g82)
    c: Block(g76)
    c: Block(g82)
    c: Coincident(g85,g76)
    c: Coincident(g85,g82)
    c: Vertical(g85)
    c: Coincident(g86,g76)
    c: Coincident(g86,g58)
    c: Coincident(g87,g58)
    c: Coincident(g87,g82)
    c: Weight(g88) = 1
    c: Equal(g88,g89)
    c: Equal(g88,g90)
    c: InternalAlignment(g88,g91)
    c: InternalAlignment(g89,g91)
    c: InternalAlignment(g90,g91)
    c: InternalAlignment(g92,g91)
    c: InternalAlignment(g93,g91)
    c: Weight(g94) = 1
    c: Equal(g94,g95)
    c: Equal(g94,g96)
    c: InternalAlignment(g94,g97)
    c: InternalAlignment(g95,g97)
    c: InternalAlignment(g96,g97)
    c: InternalAlignment(g98,g97)
    c: InternalAlignment(g99,g97)
    c: Block(g91)
    c: Block(g97)
    c: Coincident(g100,g91)
    c: Coincident(g100,g97)
    c: Vertical(g100)
    c: Coincident(g101,g91)
    c: Coincident(g101,g52)
    c: Coincident(g102,g52)
    c: Coincident(g102,g97)
    c: Weight(g103) = 1
    c: Equal(g103,g104)
    c: Equal(g103,g105)
    c: InternalAlignment(g103,g106)
    c: InternalAlignment(g104,g106)
    c: InternalAlignment(g105,g106)
    c: InternalAlignment(g107,g106)
    c: InternalAlignment(g108,g106)
    c: Weight(g109) = 1
    c: Equal(g109,g110)
    c: Equal(g109,g111)
    c: InternalAlignment(g109,g112)
    c: InternalAlignment(g110,g112)
    c: InternalAlignment(g111,g112)
    c: InternalAlignment(g113,g112)
    c: InternalAlignment(g114,g112)
    c: Block(g106)
    c: Block(g112)
    c: Coincident(g115,g106)
    c: Coincident(g115,g112)
    c: Vertical(g115)
    c: Coincident(g116,g112)
    c: Coincident(g116,g70)
    c: Coincident(g117,g70)
    c: Coincident(g117,g106)
    c: Weight(g118) = 1
    c: Equal(g118,g119)
    c: Equal(g118,g120)
    c: InternalAlignment(g118,g121)
    c: InternalAlignment(g119,g121)
    c: InternalAlignment(g120,g121)
    c: InternalAlignment(g122,g121)
    c: InternalAlignment(g123,g121)
    c: Weight(g124) = 1
    c: Equal(g124,g125)
    c: Equal(g124,g126)
    c: InternalAlignment(g124,g127)
    c: InternalAlignment(g125,g127)
    c: InternalAlignment(g126,g127)
    c: InternalAlignment(g128,g127)
    c: InternalAlignment(g129,g127)
    c: Block(g121)
    c: Block(g127)
    c: Coincident(g130,g121)
    c: Coincident(g130,g127)
    c: Vertical(g130)
    c: Coincident(g131,g127)
    c: Coincident(g131,g64)
    c: Coincident(g132,g64)
    c: Coincident(g132,g121)
    c: Weight(g133) = 1
    c: Equal(g133,g134)
    c: Equal(g133,g135)
    c: InternalAlignment(g133,g136)
    c: InternalAlignment(g134,g136)
    c: InternalAlignment(g135,g136)
    c: InternalAlignment(g137,g136)
    c: InternalAlignment(g138,g136)
    c: Weight(g139) = 1
    c: Equal(g139,g140)
    c: Equal(g139,g141)
    c: InternalAlignment(g139,g142)
    c: InternalAlignment(g140,g142)
    c: InternalAlignment(g141,g142)
    c: InternalAlignment(g143,g142)
    c: InternalAlignment(g144,g142)
    c: Weight(g145) = 1
    c: Equal(g145,g146)
    c: Equal(g145,g147)
    c: InternalAlignment(g145,g148)
    c: InternalAlignment(g146,g148)
    c: InternalAlignment(g147,g148)
    c: InternalAlignment(g149,g148)
    c: InternalAlignment(g150,g148)
    c: Weight(g151) = 1
    c: Equal(g151,g152)
    c: Equal(g151,g153)
    c: InternalAlignment(g151,g154)
    c: InternalAlignment(g152,g154)
    c: InternalAlignment(g153,g154)
    c: InternalAlignment(g155,g154)
    c: InternalAlignment(g156,g154)
    c: Block(g154)
    c: Block(g148)
    c: Block(g142)
    c: Block(g136)
    c: Coincident(g157,g31)
    c: Coincident(g157,g154)
    c: Coincident(g158,g154)
    c: Coincident(g158,g148)
    c: Horizontal(g158)
    c: Coincident(g159,g148)
    c: Coincident(g159,g31)
    c: Vertical(g159)
    c: Coincident(g160,g25)
    c: Coincident(g160,g142)
    c: Vertical(g160)
    c: Coincident(g161,g142)
    c: Coincident(g161,g136)
    c: Horizontal(g161)
    c: Coincident(g162,g136)
    c: Coincident(g162,g25)
    c: Weight(g163) = 1
    c: Equal(g163,g164)
    c: Equal(g163,g165)
    c: InternalAlignment(g163,g166)
    c: InternalAlignment(g164,g166)
    c: InternalAlignment(g165,g166)
    c: InternalAlignment(g167,g166)
    c: InternalAlignment(g168,g166)
    c: Weight(g169) = 1
    c: Equal(g169,g170)
    c: Equal(g169,g171)
    c: InternalAlignment(g169,g172)
    c: InternalAlignment(g170,g172)
    c: InternalAlignment(g171,g172)
    c: InternalAlignment(g173,g172)
    c: InternalAlignment(g174,g172)
    c: Weight(g175) = 1
    c: Equal(g175,g176)
    c: Equal(g175,g177)
    c: InternalAlignment(g175,g178)
    c: InternalAlignment(g176,g178)
    c: InternalAlignment(g177,g178)
    c: InternalAlignment(g179,g178)
    c: InternalAlignment(g180,g178)
    c: Weight(g181) = 1
    c: Equal(g181,g182)
    c: Equal(g181,g183)
    c: InternalAlignment(g181,g184)
    c: InternalAlignment(g182,g184)
    c: InternalAlignment(g183,g184)
    c: InternalAlignment(g185,g184)
    c: InternalAlignment(g186,g184)
    c: Block(g184)
    c: Block(g178)
    c: Block(g172)
    c: Block(g166)
    c: Coincident(g187,g184)
    c: Coincident(g187,g178)
    c: Horizontal(g187)
    c: Coincident(g188,g178)
    c: Coincident(g188,g13)
    c: Vertical(g188)
    c: Coincident(g189,g19)
    c: Coincident(g189,g172)
    c: Vertical(g189)
    c: Coincident(g190,g172)
    c: Coincident(g190,g166)
    c: Horizontal(g190)
    c: Coincident(g191,g166)
    c: Coincident(g191,g19)
    c: Coincident(g192,g13)
    c: Weight(g193) = 1
    c: Equal(g193,g194)
    c: Equal(g193,g195)
    c: InternalAlignment(g193,g196)
    c: InternalAlignment(g194,g196)
    c: InternalAlignment(g195,g196)
    c: InternalAlignment(g197,g196)
    c: InternalAlignment(g198,g196)
    c: Weight(g199) = 1
    c: Equal(g199,g200)
    c: Equal(g199,g201)
    c: InternalAlignment(g199,g202)
    c: InternalAlignment(g200,g202)
    c: InternalAlignment(g201,g202)
    c: InternalAlignment(g203,g202)
    c: InternalAlignment(g204,g202)
    c: Block(g202)
    c: Block(g196)
    c: Coincident(g205,g202)
    c: Coincident(g205,g37)
    c: Coincident(g206,g37)
    c: Coincident(g206,g196)
    c: Coincident(g207,g196)
    c: Coincident(g207,g202)
    c: Vertical(g207)
    c: Weight(g208) = 1
    c: Equal(g208,g209)
    c: Equal(g208,g210)
    c: InternalAlignment(g208,g211)
    c: InternalAlignment(g209,g211)
    c: InternalAlignment(g210,g211)
    c: InternalAlignment(g212,g211)
    c: InternalAlignment(g213,g211)
    c: Weight(g214) = 1
    c: Equal(g214,g215)
    c: Equal(g214,g216)
    c: InternalAlignment(g214,g217)
    c: InternalAlignment(g215,g217)
    c: InternalAlignment(g216,g217)
    c: InternalAlignment(g218,g217)
    c: InternalAlignment(g219,g217)
    c: Block(g217)
    c: Block(g211)
    c: Coincident(g220,g211)
    c: Coincident(g220,g43)
    c: Coincident(g221,g43)
    c: Coincident(g221,g217)
    c: Coincident(g222,g217)
    c: Coincident(g222,g211)
    c: Vertical(g222)
    c: Horizontal(g223)
    c: Block(g223)
    c: Vertical(g224)
    c: Block(g224)
    c: Block(g225)
    c: Weight(g226) = 1
    c: Equal(g226,g227)
    c: Equal(g226,g228)
    c: InternalAlignment(g226,g229)
    c: InternalAlignment(g227,g229)
    c: InternalAlignment(g228,g229)
    c: InternalAlignment(g230,g229)
    c: InternalAlignment(g231,g229)
    c: Weight(g232) = 1
    c: Equal(g232,g233)
    c: Equal(g232,g234)
    c: InternalAlignment(g232,g235)
    c: InternalAlignment(g233,g235)
    c: InternalAlignment(g234,g235)
    c: InternalAlignment(g236,g235)
    c: InternalAlignment(g237,g235)
    c: Weight(g238) = 1
    c: Equal(g238,g239)
    c: Equal(g238,g240)
    c: InternalAlignment(g238,g241)
    c: InternalAlignment(g239,g241)
    c: InternalAlignment(g240,g241)
    c: InternalAlignment(g242,g241)
    c: InternalAlignment(g243,g241)
    c: Weight(g244) = 1
    c: Equal(g244,g245)
    c: Equal(g244,g246)
    c: InternalAlignment(g244,g247)
    c: InternalAlignment(g245,g247)
    c: InternalAlignment(g246,g247)
    c: InternalAlignment(g248,g247)
    c: InternalAlignment(g249,g247)
    c: Block(g229)
    c: Block(g235)
    c: Block(g241)
    c: Block(g247)
    c: Coincident(g250,g235)
    c: Coincident(g250,g229)
    c: Horizontal(g250)
    c: Block(g192)
    c: Weight(g251) = 1
    c: Equal(g251,g252)
    c: Equal(g251,g253)
    c: InternalAlignment(g251,g254)
    c: InternalAlignment(g252,g254)
    c: InternalAlignment(g253,g254)
    c: InternalAlignment(g255,g254)
    c: InternalAlignment(g256,g254)
    c: Weight(g257) = 1
    c: Equal(g257,g258)
    c: Equal(g257,g259)
    c: InternalAlignment(g257,g260)
    c: InternalAlignment(g258,g260)
    c: InternalAlignment(g259,g260)
    c: InternalAlignment(g261,g260)
    c: InternalAlignment(g262,g260)
    c: Block(g254)
    c: Block(g260)
    c: Coincident(g263,g254)
    c: Coincident(g263,g260)
    c: Weight(g264) = 1
    c: Equal(g264,g265)
    c: Equal(g264,g266)
    c: InternalAlignment(g264,g267)
    c: InternalAlignment(g265,g267)
    c: InternalAlignment(g266,g267)
    c: InternalAlignment(g268,g267)
    c: InternalAlignment(g269,g267)
    c: Weight(g270) = 1
    c: Equal(g270,g271)
    c: Equal(g270,g272)
    c: InternalAlignment(g270,g273)
    c: InternalAlignment(g271,g273)
    c: InternalAlignment(g272,g273)
    c: InternalAlignment(g274,g273)
    c: InternalAlignment(g275,g273)
    c: Weight(g276) = 1
    c: Equal(g276,g277)
    c: Equal(g276,g278)
    c: InternalAlignment(g276,g279)
    c: InternalAlignment(g277,g279)
    c: InternalAlignment(g278,g279)
    c: InternalAlignment(g280,g279)
    c: InternalAlignment(g281,g279)
    c: Block(g279)
    c: Block(g273)
    c: Block(g267)
    c: Coincident(g282,g273)
    c: Coincident(g282,g267)
    c: Coincident(g283,g267)
    c: Coincident(g283,g279)
    c: Vertical(g283)
    c: Coincident(g284,g279)
    c: Coincident(g284,g273)
    c: Horizontal(g284)
    c: Weight(g285) = 1
    c: Equal(g285,g286)
    c: InternalAlignment(g285,g287)
    c: InternalAlignment(g286,g287)
    c: InternalAlignment(g288,g287)
    c: InternalAlignment(g289,g287)
    c: Weight(g290) = 1
    c: InternalAlignment(g291,g293)
    c: InternalAlignment(g292,g293)
    c: InternalAlignment(g294,g293)
    c: InternalAlignment(g295,g293)
    c: Weight(g296) = 1
    c: Equal(g296,g297)
    c: Equal(g296,g298)
    c: InternalAlignment(g296,g299)
    c: InternalAlignment(g297,g299)
    c: InternalAlignment(g298,g299)
    c: InternalAlignment(g300,g299)
    c: InternalAlignment(g301,g299)
    c: Equal(g302,g303)
    c: Equal(g302,g304)
    c: InternalAlignment(g302,g305)
    c: InternalAlignment(g303,g305)
    c: InternalAlignment(g304,g305)
    c: InternalAlignment(g306,g305)
    c: InternalAlignment(g307,g305)
    c: Block(g293)
    c: Block(g299)
    c: Block(g305)
    c: Block(g287)
    c: Coincident(g308,g287)
    c: Coincident(g308,g293)
    c: Horizontal(g308)
    c: Coincident(g309,g293)
    c: Coincident(g309,g299)
    c: Vertical(g309)
    c: Coincident(g310,g299)
    c: Coincident(g310,g305)
    c: Horizontal(g310)
    c: Coincident(g311,g305)
    c: Coincident(g311,g287)
    c: Weight(g312) = 1
    c: Equal(g312,g313)
    c: Equal(g312,g314)
    c: InternalAlignment(g312,g315)
    c: InternalAlignment(g313,g315)
    c: InternalAlignment(g314,g315)
    c: InternalAlignment(g316,g315)
    c: InternalAlignment(g317,g315)
    c: Weight(g318) = 1
    c: Equal(g318,g319)
    c: Equal(g318,g320)
    c: InternalAlignment(g318,g321)
    c: InternalAlignment(g319,g321)
    c: InternalAlignment(g320,g321)
    c: InternalAlignment(g322,g321)
    c: InternalAlignment(g323,g321)
    c: Weight(g324) = 1
    c: Equal(g324,g325)
    c: Equal(g324,g326)
    c: InternalAlignment(g324,g327)
    c: InternalAlignment(g325,g327)
    c: InternalAlignment(g326,g327)
    c: InternalAlignment(g328,g327)
    c: InternalAlignment(g329,g327)
    c: Block(g327)
    c: Block(g321)
    c: Block(g315)
    c: Coincident(g330,g327)
    c: Coincident(g330,g321)
    c: Horizontal(g330)
    c: Coincident(g331,g321)
    c: Coincident(g331,g315)
    c: Vertical(g331)
    c: Coincident(g332,g315)
    c: Coincident(g332,g327)
    c: InternalAlignment(g333,g334)
    c: InternalAlignment(g335,g334)
    c: InternalAlignment(g336,g334)
    c: Block(g334)
    c: Equal(g337,g338)
    c: Equal(g337,g339)
    c: InternalAlignment(g337,g340)
    c: InternalAlignment(g338,g340)
    c: InternalAlignment(g339,g340)
    c: InternalAlignment(g341,g340)
    c: InternalAlignment(g342,g340)
    c: Block(g340)
    c: Coincident(g343,g334)
    c: Horizontal(g343)
    c: Block(g343)
    c: Coincident(g344,g334)
    c: Coincident(g344,g260)
    c: Vertical(g344)
    c: Coincident(g345,g340)
    c: Coincident(g345,g254)
    c: Vertical(g345)
    c: Coincident(g347,g5)
    c: Coincident(g348,g5)
    c: Block(g346)
    c: Block(g5)
    c: Block(g348)
    c: Block(g347)
    c: Distance(g344) = 119.89
FEATURE [Sketcher::SketchObject] Sketch001
  FullyConstrained = true
  MapMode = 4
  Placement = pos=(0,0,0) rot=(0.57735,0.57735,0.57735;2.0944rad)
  Support = -> [Sketch]
  sketch-geometry (46):
    g0: BSplineCurve PolesCount=3 KnotsCount=2 Degree=2 IsPeriodic=0
    g1: ArcOfCircle CenterX=73.1223 CenterY=-32.291 CenterZ=0 NormalX=0 NormalY=0 NormalZ=1 AngleXU=0 Radius=13 StartAngle=5.92268 EndAngle=9.06428
    g2: ArcOfCircle CenterX=66.7816 CenterY=-49.1439 CenterZ=0 NormalX=0 NormalY=0 NormalZ=1 AngleXU=0 Radius=13 StartAngle=2.78068 EndAngle=5.92131
    g3: ArcOfCircle CenterX=55.9263 CenterY=-78.1807 CenterZ=0 NormalX=0 NormalY=0 NormalZ=1 AngleXU=0 Radius=13 StartAngle=5.92268 EndAngle=9.06428
    g4: ArcOfCircle CenterX=49.5884 CenterY=-95.0342 CenterZ=0 NormalX=0 NormalY=0 NormalZ=1 AngleXU=0 Radius=13 StartAngle=2.78068 EndAngle=5.92131
    g5: ArcOfCircle CenterX=38.7206 CenterY=-124.067 CenterZ=0 NormalX=0 NormalY=0 NormalZ=1 AngleXU=0 Radius=13 StartAngle=5.92268 EndAngle=9.06428
    g6: ArcOfCircle CenterX=32.3875 CenterY=-140.92 CenterZ=0 NormalX=0 NormalY=0 NormalZ=1 AngleXU=0 Radius=13 StartAngle=2.78068 EndAngle=5.92131
    g7: ArcOfCircle CenterX=21.4715 CenterY=-169.934 CenterZ=0 NormalX=0 NormalY=0 NormalZ=1 AngleXU=0 Radius=13 StartAngle=5.92268 EndAngle=9.06428
    g8: ArcOfCircle CenterX=15.1336 CenterY=-186.787 CenterZ=0 NormalX=0 NormalY=0 NormalZ=1 AngleXU=0 Radius=13 StartAngle=2.78068 EndAngle=5.92131
    g9-g12: Circle x4 (B-spline internal-alignment scaffolding for g13; pole/knot coordinates omitted)
    g13: BSplineCurve PolesCount=4 KnotsCount=2 Degree=3 IsPeriodic=0
    g14: GeomPoint X=28.8094 Y=-19.0875 Z=0
    g15: GeomPoint X=47.0443 Y=-50.4712 Z=0
    g16: Circle CenterX=53.5586 CenterY=-23.2695 CenterZ=0 NormalX=0 NormalY=0 NormalZ=1 AngleXU=0 Radius=3.24518
    g17: Circle CenterX=-195.441 CenterY=-127.082 CenterZ=0 NormalX=0 NormalY=0 NormalZ=1 AngleXU=0 Radius=1
    g18: Circle CenterX=-8.24091 CenterY=-197.481 CenterZ=0 NormalX=0 NormalY=0 NormalZ=1 AngleXU=0 Radius=1
    g19: Circle CenterX=12.8789 CenterY=-141.321 CenterZ=0 NormalX=0 NormalY=0 NormalZ=1 AngleXU=0 Radius=1
    g20: BSplineCurve PolesCount=3 KnotsCount=2 Degree=2 IsPeriodic=0
    g21: GeomPoint X=-195.441 Y=-127.082 Z=0
    g22: GeomPoint X=12.8789 Y=-141.321 Z=0
    g23: Circle CenterX=-12.8016 CenterY=-179.036 CenterZ=0 NormalX=0 NormalY=0 NormalZ=1 AngleXU=0 Radius=10.5072
    g24: Circle CenterX=0.933922 CenterY=-166.43 CenterZ=0 NormalX=0 NormalY=0 NormalZ=1 AngleXU=0 Radius=3.26661
    g25: Circle CenterX=-33.5518 CenterY=-176.44 CenterZ=0 NormalX=0 NormalY=0 NormalZ=1 AngleXU=0 Radius=5.64388
    g26: Circle CenterX=-47.2366 CenterY=-173.859 CenterZ=0 NormalX=0 NormalY=0 NormalZ=1 AngleXU=0 Radius=3.01653
    g27: Circle CenterX=-56.2595 CenterY=-171.456 CenterZ=0 NormalX=0 NormalY=0 NormalZ=1 AngleXU=0 Radius=2.12826
    g28: ArcOfCircle CenterX=51.2151 CenterY=-198.473 CenterZ=0 NormalX=0 NormalY=0 NormalZ=1 AngleXU=0 Radius=20 StartAngle=2.78189 EndAngle=4.35269
    g29: LineSegment StartX=32.4951 StartY=-191.433 StartZ=0 EndX=94.6578 EndY=-26.1352 EndZ=0
    g30: LineSegment StartX=43.1192 StartY=-220.001 StartZ=0 EndX=-196.497 EndY=-129.89 EndZ=0
    g31: LineSegment StartX=43.1192 StartY=-220.001 StartZ=0 EndX=44.1752 EndY=-217.193 EndZ=0
    g32: LineSegment StartX=117.223 StartY=-19.0875 StartZ=0 EndX=117.223 EndY=-16.0875 EndZ=0
    g33: LineSegment StartX=117.223 StartY=-16.0875 StartZ=0 EndX=17.2232 EndY=-16.0875 EndZ=0
    g34: LineSegment StartX=17.2232 StartY=-16.0875 StartZ=0 EndX=17.2232 EndY=-19.0875 EndZ=0
    g35: LineSegment StartX=28.8094 StartY=-19.0875 StartZ=0 EndX=17.2232 EndY=-19.0875 EndZ=0
    g36: LineSegment StartX=47.0443 StartY=-50.4712 StartZ=0 EndX=12.8789 EndY=-141.321 EndZ=0
    g37: LineSegment StartX=-195.441 StartY=-127.082 StartZ=0 EndX=-196.497 EndY=-129.89 EndZ=0
    g38: LineSegment StartX=85.2866 StartY=-36.8766 StartZ=0 EndX=78.9396 EndY=-53.7463 EndZ=0
    g39: LineSegment StartX=60.9579 StartY=-27.7053 StartZ=0 EndX=54.6191 EndY=-44.5532 EndZ=0
    g40: LineSegment StartX=68.0907 StartY=-82.7664 StartZ=0 EndX=61.7465 EndY=-99.6365 EndZ=0
    g41: LineSegment StartX=43.7619 StartY=-73.595 StartZ=0 EndX=37.426 EndY=-90.4435 EndZ=0
    g42: LineSegment StartX=50.885 StartY=-128.652 StartZ=0 EndX=44.5456 EndY=-145.522 EndZ=0
    g43: LineSegment StartX=26.5562 StartY=-119.481 StartZ=0 EndX=20.2251 EndY=-136.329 EndZ=0
    g44: LineSegment StartX=9.3071 StartY=-165.349 StartZ=0 EndX=2.97115 EndY=-182.197 EndZ=0
    g45: LineSegment StartX=33.6358 StartY=-174.52 StartZ=0 EndX=27.2917 EndY=-191.39 EndZ=0
  constraints (71):
    c: Block(g0)
    c: Block(g1)
    c: Block(g2)
    c: Block(g4)
    c: Block(g3)
    c: Block(g6)
    c: Block(g5)
    c: Block(g8)
    c: Block(g7)
    c: Weight(g9) = 1
    c: Equal(g9,g10)
    c: Equal(g9,g11)
    c: Equal(g9,g12)
    c: InternalAlignment(g9-g12 -> g13) x4
    c: InternalAlignment(g14,g13)
    c: InternalAlignment(g15,g13)
    c: Block(g16)
    c: Weight(g17) = 1
    c: Equal(g17,g18)
    c: Equal(g17,g19)
    c: InternalAlignment(g17,g20)
    c: InternalAlignment(g18,g20)
    c: InternalAlignment(g19,g20)
    c: InternalAlignment(g21,g20)
    c: InternalAlignment(g22,g20)
    c: Block(g20)
    c: Block(g23)
    c: Block(g24)
    c: Block(g25)
    c: Block(g26)
    c: Block(g27)
    c: Block(g28)
    c: Coincident(g29,g28)
    c: Coincident(g29,g0)
    c: Block(g13)
    c: Coincident(g31,g30)
    c: Coincident(g31,g28)
    c: Block(g31)
    c: Coincident(g32,g0)
    c: Vertical(g32)
    c: Coincident(g33,g32)
    c: Horizontal(g33)
    c: Coincident(g34,g33)
    c: Vertical(g34)
    c: Block(g33)
    c: Coincident(g35,g13)
    c: Coincident(g35,g34)
    c: Horizontal(g35)
    c: Coincident(g36,g13)
    c: Coincident(g36,g20)
    c: Coincident(g37,g20)
    c: Coincident(g37,g30)
    c: Block(g30)
    c: Coincident(g38,g1)
    c: Coincident(g38,g2)
    c: Coincident(g39,g1)
    c: Coincident(g39,g2)
    c: Coincident(g40,g3)
    c: Coincident(g40,g4)
    c: Coincident(g41,g3)
    c: Coincident(g41,g4)
    c: Coincident(g42,g5)
    c: Coincident(g42,g6)
    c: Coincident(g43,g5)
    c: Coincident(g43,g6)
    c: Coincident(g44,g7)
    c: Coincident(g44,g8)
    c: Coincident(g45,g7)
    c: Coincident(g45,g8)
    c: Distance(g30) = 256
    c: Distance(g33) = 100
FEATURE [Part::Extrusion] Extrude002
  Base = -> Sketch001
  Dir = (1,0,0)
  DirMode = 2
  FaceMakerClass = Part::FaceMakerBullseye
  LengthFwd = 8
  LengthRev = 0
  Solid = true
  Symmetric = false
FEATURE [Sketcher::SketchObject] Sketch002
  FullyConstrained = true
  sketch-geometry (20):
    g0: LineSegment StartX=-2.77179 StartY=-200.304 StartZ=0 EndX=5.22821 EndY=-200.304 EndZ=0
    g1: LineSegment StartX=5.22821 StartY=-200.304 StartZ=0 EndX=5.22821 EndY=-197.304 EndZ=0
    g2: LineSegment StartX=-2.77179 StartY=-200.304 StartZ=0 EndX=-2.77179 EndY=-197.304 EndZ=0
    g3: LineSegment StartX=5.22821 StartY=-197.304 StartZ=0 EndX=8.22821 EndY=-197.304 EndZ=0
    g4: LineSegment StartX=-2.77179 StartY=-197.304 StartZ=0 EndX=-5.77179 EndY=-197.304 EndZ=0
    g5: LineSegment StartX=19.2282 StartY=-203.304 StartZ=0 EndX=19.2282 EndY=-206.304 EndZ=0
    g6: LineSegment StartX=-16.7718 StartY=-203.304 StartZ=0 EndX=-16.7718 EndY=-206.304 EndZ=0
    g7: LineSegment StartX=-16.7718 StartY=-206.304 StartZ=0 EndX=19.2282 EndY=-206.304 EndZ=0
    g8: Circle CenterX=-16.7718 CenterY=-203.304 CenterZ=0 NormalX=0 NormalY=0 NormalZ=1 AngleXU=0 Radius=1
    g9: Circle CenterX=-5.77179 CenterY=-203.304 CenterZ=0 NormalX=0 NormalY=0 NormalZ=1 AngleXU=0 Radius=1
    g10: Circle CenterX=-5.77179 CenterY=-197.304 CenterZ=0 NormalX=0 NormalY=0 NormalZ=1 AngleXU=0 Radius=1
    g11: BSplineCurve PolesCount=3 KnotsCount=2 Degree=2 IsPeriodic=0
    g12: GeomPoint X=-16.7718 Y=-203.304 Z=0
    g13: GeomPoint X=-5.77179 Y=-197.304 Z=0
    g14: Circle CenterX=19.2282 CenterY=-203.304 CenterZ=0 NormalX=0 NormalY=0 NormalZ=1 AngleXU=0 Radius=1
    g15: Circle CenterX=8.22821 CenterY=-203.304 CenterZ=0 NormalX=0 NormalY=0 NormalZ=1 AngleXU=0 Radius=1
    g16: Circle CenterX=8.22821 CenterY=-197.304 CenterZ=0 NormalX=0 NormalY=0 NormalZ=1 AngleXU=0 Radius=1
    g17: BSplineCurve PolesCount=3 KnotsCount=2 Degree=2 IsPeriodic=0
    g18: GeomPoint X=19.2282 Y=-203.304 Z=0
    g19: GeomPoint X=8.22821 Y=-197.304 Z=0
  constraints (41):
    c: Horizontal(g0)
    c: Distance(g0) = 8
    c: Coincident(g1,g0)
    c: Vertical(g1)
    c: Distance(g1) = 3
    c: Coincident(g2,g0)
    c: Vertical(g2)
    c: Distance(g2) = 3
    c: Coincident(g3,g1)
    c: Horizontal(g3)
    c: Distance(g3) = 3
    c: Coincident(g4,g2)
    c: Horizontal(g4)
    c: Distance(g4) = 3
    c: Vertical(g5)
    c: Vertical(g6)
    c: Coincident(g7,g6)
    c: Coincident(g7,g5)
    c: Weight(g8) = 1
    c: Equal(g8,g9)
    c: Equal(g8,g10)
    c: Coincident(g11,g4)
    c: InternalAlignment(g8,g11)
    c: InternalAlignment(g9,g11)
    c: InternalAlignment(g10,g11)
    c: InternalAlignment(g12,g11)
    c: InternalAlignment(g13,g11)
    c: Coincident(g17,g5)
    c: Weight(g14) = 1
    c: Equal(g14,g15)
    c: Equal(g14,g16)
    c: Coincident(g17,g3)
    c: InternalAlignment(g14,g17)
    c: InternalAlignment(g15,g17)
    c: InternalAlignment(g16,g17)
    c: InternalAlignment(g18,g17)
    c: InternalAlignment(g19,g17)
    c: Block(g7)
    c: Block(g17)
    c: Block(g11)
    c: Block(g6)
FEATURE [Part::Extrusion] Extrude003
  Base = -> Sketch002
  Dir = (0,0,1)
  DirMode = 2
  FaceMakerClass = Part::FaceMakerBullseye
  LengthFwd = 260
  LengthRev = 0
  Solid = true
  Symmetric = false
FEATURE [Part::Extrusion] Extrude
  Base = -> Sketch
  Dir = (0,0,1)
  DirMode = 2
  FaceMakerClass = Part::FaceMakerBullseye
  LengthFwd = 14
  LengthRev = 0
  Solid = true
  Symmetric = false
FEATURE [Sketcher::SketchObject] Sketch003
  FullyConstrained = false
  sketch-geometry (349):
    g0: LineSegment StartX=-10.9272 StartY=-82.7794 StartZ=0 EndX=46.0728 EndY=-51.4823 EndZ=0
    g1: LineSegment StartX=-10.9272 StartY=76.4095 StartZ=0 EndX=-10.9272 EndY=-82.7794 EndZ=0
    g2: LineSegment StartX=46.0728 StartY=76.4095 StartZ=0 EndX=46.0728 EndY=-51.4823 EndZ=0
    g3: LineSegment StartX=-42.9272 StartY=136.221 StartZ=0 EndX=-42.9272 EndY=-103.779 EndZ=0
    g4: LineSegment StartX=407.073 StartY=136.221 StartZ=0 EndX=407.073 EndY=-103.779 EndZ=0
    g5: ArcOfCircle CenterX=-26.9272 CenterY=-83.7794 CenterZ=0 NormalX=0 NormalY=0 NormalZ=1 AngleXU=0 Radius=8 StartAngle=3.14159 EndAngle=6.28319
    g6: ArcOfCircle CenterX=391.073 CenterY=-83.7794 CenterZ=0 NormalX=0 NormalY=0 NormalZ=1 AngleXU=0 Radius=8 StartAngle=3.14159 EndAngle=6.28319
    g7: Circle CenterX=175.022 CenterY=27.0628 CenterZ=0 NormalX=0 NormalY=0 NormalZ=1 AngleXU=0 Radius=1
    g8: Circle CenterX=179.022 CenterY=24.8665 CenterZ=0 NormalX=0 NormalY=0 NormalZ=1 AngleXU=0 Radius=1
    g9: Circle CenterX=179.022 CenterY=27.0628 CenterZ=0 NormalX=0 NormalY=0 NormalZ=1 AngleXU=0 Radius=1
    g10: BSplineCurve PolesCount=3 KnotsCount=2 Degree=2 IsPeriodic=0
    g11: GeomPoint X=175.022 Y=27.0628 Z=0
    g12: GeomPoint X=179.022 Y=27.0628 Z=0
    g13: Circle CenterX=189.124 CenterY=27.0628 CenterZ=0 NormalX=0 NormalY=0 NormalZ=1 AngleXU=0 Radius=1
    g14: Circle CenterX=185.124 CenterY=24.8665 CenterZ=0 NormalX=0 NormalY=0 NormalZ=1 AngleXU=0 Radius=1
    g15: Circle CenterX=185.124 CenterY=27.0628 CenterZ=0 NormalX=0 NormalY=0 NormalZ=1 AngleXU=0 Radius=1
    g16: BSplineCurve PolesCount=3 KnotsCount=2 Degree=2 IsPeriodic=0
    g17: GeomPoint X=189.124 Y=27.0628 Z=0
    g18: GeomPoint X=185.124 Y=27.0628 Z=0
    g19: Circle CenterX=175.022 CenterY=5.37834 CenterZ=0 NormalX=0 NormalY=0 NormalZ=1 AngleXU=0 Radius=1
    g20: Circle CenterX=179.022 CenterY=7.57463 CenterZ=0 NormalX=0 NormalY=0 NormalZ=1 AngleXU=0 Radius=1
    g21: Circle CenterX=179.022 CenterY=5.34704 CenterZ=0 NormalX=0 NormalY=0 NormalZ=1 AngleXU=0 Radius=1
    g22: BSplineCurve PolesCount=3 KnotsCount=2 Degree=2 IsPeriodic=0
    g23: GeomPoint X=175.022 Y=5.37834 Z=0
    g24: GeomPoint X=179.022 Y=5.34704 Z=0
    g25: Circle CenterX=189.124 CenterY=5.37834 CenterZ=0 NormalX=0 NormalY=0 NormalZ=1 AngleXU=0 Radius=1
    g26: Circle CenterX=185.124 CenterY=7.57463 CenterZ=0 NormalX=0 NormalY=0 NormalZ=1 AngleXU=0 Radius=1
    g27: Circle CenterX=185.124 CenterY=5.34704 CenterZ=0 NormalX=0 NormalY=0 NormalZ=1 AngleXU=0 Radius=1
    g28: BSplineCurve PolesCount=3 KnotsCount=2 Degree=2 IsPeriodic=0
    g29: GeomPoint X=189.124 Y=5.37834 Z=0
    g30: GeomPoint X=185.124 Y=5.34704 Z=0
    g31: Circle CenterX=165.871 CenterY=18.1458 CenterZ=0 NormalX=0 NormalY=0 NormalZ=1 AngleXU=0 Radius=1
    g32: Circle CenterX=169.377 CenterY=16.2206 CenterZ=0 NormalX=0 NormalY=0 NormalZ=1 AngleXU=0 Radius=1
    g33: Circle CenterX=165.871 CenterY=14.2954 CenterZ=0 NormalX=0 NormalY=0 NormalZ=1 AngleXU=0 Radius=1
    g34: BSplineCurve PolesCount=3 KnotsCount=2 Degree=2 IsPeriodic=0
    g35: GeomPoint X=165.871 Y=18.1458 Z=0
    g36: GeomPoint X=165.871 Y=14.2954 Z=0
    g37: Circle CenterX=198.275 CenterY=18.1458 CenterZ=0 NormalX=0 NormalY=0 NormalZ=1 AngleXU=0 Radius=1
    g38: Circle CenterX=194.768 CenterY=16.2206 CenterZ=0 NormalX=0 NormalY=0 NormalZ=1 AngleXU=0 Radius=1
    g39: Circle CenterX=198.275 CenterY=14.2954 CenterZ=0 NormalX=0 NormalY=0 NormalZ=1 AngleXU=0 Radius=1
    g40: BSplineCurve PolesCount=3 KnotsCount=2 Degree=2 IsPeriodic=0
    g41: GeomPoint X=198.275 Y=18.1458 Z=0
    g42: GeomPoint X=198.275 Y=14.2954 Z=0
    g43: LineSegment StartX=407.073 StartY=-103.779 StartZ=0 EndX=-42.9272 EndY=-103.779 EndZ=0
    g44: LineSegment StartX=407.073 StartY=136.221 StartZ=0 EndX=-42.9272 EndY=136.221 EndZ=0
    g45: LineSegment StartX=46.0728 StartY=76.4095 StartZ=0 EndX=-10.9272 EndY=76.4095 EndZ=0
    g46: Circle CenterX=125.607 CenterY=54.1951 CenterZ=0 NormalX=0 NormalY=0 NormalZ=1 AngleXU=0 Radius=1
    g47: Circle CenterX=139.632 CenterY=46.4944 CenterZ=0 NormalX=0 NormalY=0 NormalZ=1 AngleXU=0 Radius=1
    g48: Circle CenterX=127.326 CenterY=56.7187 CenterZ=0 NormalX=0 NormalY=0 NormalZ=1 AngleXU=0 Radius=1
    g49: BSplineCurve PolesCount=3 KnotsCount=2 Degree=2 IsPeriodic=0
    g50: GeomPoint X=125.607 Y=54.1951 Z=0
    g51: GeomPoint X=127.326 Y=56.7187 Z=0
    g52: Circle CenterX=236.821 CenterY=56.7187 CenterZ=0 NormalX=0 NormalY=0 NormalZ=1 AngleXU=0 Radius=1
    g53: Circle CenterX=224.513 CenterY=46.4944 CenterZ=0 NormalX=0 NormalY=0 NormalZ=1 AngleXU=0 Radius=1
    g54: Circle CenterX=238.538 CenterY=54.1951 CenterZ=0 NormalX=0 NormalY=0 NormalZ=1 AngleXU=0 Radius=1
    g55: BSplineCurve PolesCount=3 KnotsCount=2 Degree=2 IsPeriodic=0
    g56: GeomPoint X=236.821 Y=56.7187 Z=0
    g57: GeomPoint X=238.538 Y=54.1951 Z=0
    g58: Circle CenterX=238.538 CenterY=-21.7539 CenterZ=0 NormalX=0 NormalY=0 NormalZ=1 AngleXU=0 Radius=1
    g59: Circle CenterX=224.513 CenterY=-14.0532 CenterZ=0 NormalX=0 NormalY=0 NormalZ=1 AngleXU=0 Radius=1
    g60: Circle CenterX=236.821 CenterY=-24.2775 CenterZ=0 NormalX=0 NormalY=0 NormalZ=1 AngleXU=0 Radius=1
    g61: BSplineCurve PolesCount=3 KnotsCount=2 Degree=2 IsPeriodic=0
    g62: GeomPoint X=238.538 Y=-21.7539 Z=0
    g63: GeomPoint X=236.821 Y=-24.2775 Z=0
    g64: Circle CenterX=125.607 CenterY=-21.7539 CenterZ=0 NormalX=0 NormalY=0 NormalZ=1 AngleXU=0 Radius=1
    g65: Circle CenterX=139.632 CenterY=-14.0532 CenterZ=0 NormalX=0 NormalY=0 NormalZ=1 AngleXU=0 Radius=1
    g66: Circle CenterX=127.325 CenterY=-24.2775 CenterZ=0 NormalX=0 NormalY=0 NormalZ=1 AngleXU=0 Radius=1
    g67: BSplineCurve PolesCount=3 KnotsCount=2 Degree=2 IsPeriodic=0
    g68: GeomPoint X=125.607 Y=-21.7539 Z=0
    g69: GeomPoint X=127.325 Y=-24.2775 Z=0
    g70: Circle CenterX=302.996 CenterY=111.695 CenterZ=0 NormalX=0 NormalY=0 NormalZ=1 AngleXU=0 Radius=1
    g71: Circle CenterX=306.073 CenterY=114.251 CenterZ=0 NormalX=0 NormalY=0 NormalZ=1 AngleXU=0 Radius=1
    g72: Circle CenterX=306.073 CenterY=110.251 CenterZ=0 NormalX=0 NormalY=0 NormalZ=1 AngleXU=0 Radius=1
    g73: BSplineCurve PolesCount=3 KnotsCount=2 Degree=2 IsPeriodic=0
    g74: GeomPoint X=302.996 Y=111.695 Z=0
    g75: GeomPoint X=306.073 Y=110.251 Z=0
    g76: Circle CenterX=306.073 CenterY=95.2763 CenterZ=0 NormalX=0 NormalY=0 NormalZ=1 AngleXU=0 Radius=1
    g77: Circle CenterX=306.073 CenterY=91.2763 CenterZ=0 NormalX=0 NormalY=0 NormalZ=1 AngleXU=0 Radius=1
    g78: Circle CenterX=302.567 CenterY=89.3511 CenterZ=0 NormalX=0 NormalY=0 NormalZ=1 AngleXU=0 Radius=1
    g79: BSplineCurve PolesCount=3 KnotsCount=2 Degree=2 IsPeriodic=0
    g80: GeomPoint X=306.073 Y=95.2763 Z=0
    g81: GeomPoint X=302.567 Y=89.3511 Z=0
    g82: LineSegment StartX=306.073 StartY=110.251 StartZ=0 EndX=306.073 EndY=95.2763 EndZ=0
    g83: LineSegment StartX=302.996 StartY=111.695 StartZ=0 EndX=236.821 EndY=56.7187 EndZ=0
    g84: LineSegment StartX=238.538 StartY=54.1951 StartZ=0 EndX=302.567 EndY=89.3511 EndZ=0
    g85: Circle CenterX=61.1496 CenterY=111.695 CenterZ=0 NormalX=0 NormalY=0 NormalZ=1 AngleXU=0 Radius=1
    g86: Circle CenterX=58.0728 CenterY=114.251 CenterZ=0 NormalX=0 NormalY=0 NormalZ=1 AngleXU=0 Radius=1
    g87: Circle CenterX=58.0728 CenterY=110.251 CenterZ=0 NormalX=0 NormalY=0 NormalZ=1 AngleXU=0 Radius=1
    g88: BSplineCurve PolesCount=3 KnotsCount=2 Degree=2 IsPeriodic=0
    g89: GeomPoint X=61.1496 Y=111.695 Z=0
    g90: GeomPoint X=58.0728 Y=110.251 Z=0
    g91: Circle CenterX=61.5791 CenterY=89.3511 CenterZ=0 NormalX=0 NormalY=0 NormalZ=1 AngleXU=0 Radius=1
    g92: Circle CenterX=58.0728 CenterY=91.2763 CenterZ=0 NormalX=0 NormalY=0 NormalZ=1 AngleXU=0 Radius=1
    g93: Circle CenterX=58.0728 CenterY=95.2763 CenterZ=0 NormalX=0 NormalY=0 NormalZ=1 AngleXU=0 Radius=1
    g94: BSplineCurve PolesCount=3 KnotsCount=2 Degree=2 IsPeriodic=0
    g95: GeomPoint X=61.5791 Y=89.3511 Z=0
    g96: GeomPoint X=58.0728 Y=95.2763 Z=0
    g97: LineSegment StartX=58.0728 StartY=110.251 StartZ=0 EndX=58.0728 EndY=95.2763 EndZ=0
    g98: LineSegment StartX=61.1496 StartY=111.695 StartZ=0 EndX=127.326 EndY=56.7187 EndZ=0
    g99: LineSegment StartX=125.607 StartY=54.1951 StartZ=0 EndX=61.5791 EndY=89.3511 EndZ=0
    g100: Circle CenterX=61.5791 CenterY=-56.9099 CenterZ=0 NormalX=0 NormalY=0 NormalZ=1 AngleXU=0 Radius=1
    g101: Circle CenterX=58.0728 CenterY=-58.8351 CenterZ=0 NormalX=0 NormalY=0 NormalZ=1 AngleXU=0 Radius=1
    g102: Circle CenterX=58.0728 CenterY=-62.8351 CenterZ=0 NormalX=0 NormalY=0 NormalZ=1 AngleXU=0 Radius=1
    g103: BSplineCurve PolesCount=3 KnotsCount=2 Degree=2 IsPeriodic=0
    g104: GeomPoint X=61.5791 Y=-56.9099 Z=0
    g105: GeomPoint X=58.0728 Y=-62.8351 Z=0
    g106: Circle CenterX=58.0728 CenterY=-77.8102 CenterZ=0 NormalX=0 NormalY=0 NormalZ=1 AngleXU=0 Radius=1
    g107: Circle CenterX=58.0728 CenterY=-81.8102 CenterZ=0 NormalX=0 NormalY=0 NormalZ=1 AngleXU=0 Radius=1
    g108: Circle CenterX=61.1496 CenterY=-79.2541 CenterZ=0 NormalX=0 NormalY=0 NormalZ=1 AngleXU=0 Radius=1
    g109: BSplineCurve PolesCount=3 KnotsCount=2 Degree=2 IsPeriodic=0
    g110: GeomPoint X=58.0728 Y=-77.8102 Z=0
    g111: GeomPoint X=61.1496 Y=-79.2541 Z=0
    g112: LineSegment StartX=58.0728 StartY=-62.8351 StartZ=0 EndX=58.0728 EndY=-77.8102 EndZ=0
    g113: LineSegment StartX=61.1496 StartY=-79.2541 StartZ=0 EndX=127.325 EndY=-24.2775 EndZ=0
    g114: LineSegment StartX=125.607 StartY=-21.7539 StartZ=0 EndX=61.5791 EndY=-56.9099 EndZ=0
    g115: Circle CenterX=302.567 CenterY=-56.9099 CenterZ=0 NormalX=0 NormalY=0 NormalZ=1 AngleXU=0 Radius=1
    g116: Circle CenterX=306.073 CenterY=-58.8351 CenterZ=0 NormalX=0 NormalY=0 NormalZ=1 AngleXU=0 Radius=1
    g117: Circle CenterX=306.073 CenterY=-62.8351 CenterZ=0 NormalX=0 NormalY=0 NormalZ=1 AngleXU=0 Radius=1
    g118: BSplineCurve PolesCount=3 KnotsCount=2 Degree=2 IsPeriodic=0
    g119: GeomPoint X=302.567 Y=-56.9099 Z=0
    g120: GeomPoint X=306.073 Y=-62.8351 Z=0
    g121: Circle CenterX=302.996 CenterY=-79.2541 CenterZ=0 NormalX=0 NormalY=0 NormalZ=1 AngleXU=0 Radius=1
    g122: Circle CenterX=306.073 CenterY=-81.8102 CenterZ=0 NormalX=0 NormalY=0 NormalZ=1 AngleXU=0 Radius=1
    g123: Circle CenterX=306.073 CenterY=-77.8102 CenterZ=0 NormalX=0 NormalY=0 NormalZ=1 AngleXU=0 Radius=1
    g124: BSplineCurve PolesCount=3 KnotsCount=2 Degree=2 IsPeriodic=0
    g125: GeomPoint X=302.996 Y=-79.2541 Z=0
    g126: GeomPoint X=306.073 Y=-77.8102 Z=0
    g127: LineSegment StartX=306.073 StartY=-62.8351 StartZ=0 EndX=306.073 EndY=-77.8102 EndZ=0
    g128: LineSegment StartX=302.996 StartY=-79.2541 StartZ=0 EndX=236.821 EndY=-24.2775 EndZ=0
    g129: LineSegment StartX=238.538 StartY=-21.7539 StartZ=0 EndX=302.567 EndY=-56.9099 EndZ=0
    g130: Circle CenterX=61.6457 CenterY=-88.8112 CenterZ=0 NormalX=0 NormalY=0 NormalZ=1 AngleXU=0 Radius=1
    g131: Circle CenterX=58.0728 CenterY=-91.7794 CenterZ=0 NormalX=0 NormalY=0 NormalZ=1 AngleXU=0 Radius=1
    g132: Circle CenterX=63.9135 CenterY=-91.7794 CenterZ=0 NormalX=0 NormalY=0 NormalZ=1 AngleXU=0 Radius=1
    g133: BSplineCurve PolesCount=3 KnotsCount=2 Degree=2 IsPeriodic=0
    g134: GeomPoint X=61.6457 Y=-88.8112 Z=0
    g135: GeomPoint X=63.9135 Y=-91.7794 Z=0
    g136: Circle CenterX=179.022 CenterY=-85.8163 CenterZ=0 NormalX=0 NormalY=0 NormalZ=1 AngleXU=0 Radius=1
    g137: Circle CenterX=179.022 CenterY=-91.7794 CenterZ=0 NormalX=0 NormalY=0 NormalZ=1 AngleXU=0 Radius=1
    g138: Circle CenterX=171.895 CenterY=-91.7794 CenterZ=0 NormalX=0 NormalY=0 NormalZ=1 AngleXU=0 Radius=1
    g139: BSplineCurve PolesCount=3 KnotsCount=2 Degree=2 IsPeriodic=0
    g140: GeomPoint X=179.022 Y=-85.8163 Z=0
    g141: GeomPoint X=171.895 Y=-91.7794 Z=0
    g142: Circle CenterX=185.124 CenterY=-86.2028 CenterZ=0 NormalX=0 NormalY=0 NormalZ=1 AngleXU=0 Radius=1
    g143: Circle CenterX=185.124 CenterY=-91.7794 CenterZ=0 NormalX=0 NormalY=0 NormalZ=1 AngleXU=0 Radius=1
    g144: Circle CenterX=191.747 CenterY=-91.7794 CenterZ=0 NormalX=0 NormalY=0 NormalZ=1 AngleXU=0 Radius=1
    g145: BSplineCurve PolesCount=3 KnotsCount=2 Degree=2 IsPeriodic=0
    g146: GeomPoint X=185.124 Y=-86.2028 Z=0
    g147: GeomPoint X=191.747 Y=-91.7794 Z=0
    g148: Circle CenterX=299.888 CenterY=-86.6413 CenterZ=0 NormalX=0 NormalY=0 NormalZ=1 AngleXU=0 Radius=1
    g149: Circle CenterX=306.073 CenterY=-91.7794 CenterZ=0 NormalX=0 NormalY=0 NormalZ=1 AngleXU=0 Radius=1
    g150: Circle CenterX=298.776 CenterY=-91.7794 CenterZ=0 NormalX=0 NormalY=0 NormalZ=1 AngleXU=0 Radius=1
    g151: BSplineCurve PolesCount=3 KnotsCount=2 Degree=2 IsPeriodic=0
    g152: GeomPoint X=299.888 Y=-86.6413 Z=0
    g153: GeomPoint X=298.776 Y=-91.7794 Z=0
    g154: LineSegment StartX=189.124 StartY=5.37834 StartZ=0 EndX=299.888 EndY=-86.6413 EndZ=0
    g155: LineSegment StartX=298.776 StartY=-91.7794 StartZ=0 EndX=191.747 EndY=-91.7794 EndZ=0
    g156: LineSegment StartX=185.124 StartY=-86.2028 StartZ=0 EndX=185.124 EndY=5.34704 EndZ=0
    g157: LineSegment StartX=179.022 StartY=5.34704 StartZ=0 EndX=179.022 EndY=-85.8163 EndZ=0
    g158: LineSegment StartX=171.895 StartY=-91.7794 StartZ=0 EndX=63.9135 EndY=-91.7794 EndZ=0
    g159: LineSegment StartX=61.6457 StartY=-88.8112 StartZ=0 EndX=175.022 EndY=5.37834 EndZ=0
    g160: Circle CenterX=302.073 CenterY=124.221 CenterZ=0 NormalX=0 NormalY=0 NormalZ=1 AngleXU=0 Radius=1
    g161: Circle CenterX=306.073 CenterY=124.221 CenterZ=0 NormalX=0 NormalY=0 NormalZ=1 AngleXU=0 Radius=1
    g162: Circle CenterX=302.996 CenterY=121.665 CenterZ=0 NormalX=0 NormalY=0 NormalZ=1 AngleXU=0 Radius=1
    g163: BSplineCurve PolesCount=3 KnotsCount=2 Degree=2 IsPeriodic=0
    g164: GeomPoint X=302.073 Y=124.221 Z=0
    g165: GeomPoint X=302.996 Y=121.665 Z=0
    g166: Circle CenterX=189.124 CenterY=124.221 CenterZ=0 NormalX=0 NormalY=0 NormalZ=1 AngleXU=0 Radius=1
    g167: Circle CenterX=185.124 CenterY=124.221 CenterZ=0 NormalX=0 NormalY=0 NormalZ=1 AngleXU=0 Radius=1
    g168: Circle CenterX=185.124 CenterY=120.221 CenterZ=0 NormalX=0 NormalY=0 NormalZ=1 AngleXU=0 Radius=1
    g169: BSplineCurve PolesCount=3 KnotsCount=2 Degree=2 IsPeriodic=0
    g170: GeomPoint X=189.124 Y=124.221 Z=0
    g171: GeomPoint X=185.124 Y=120.221 Z=0
    g172: Circle CenterX=175.022 CenterY=124.221 CenterZ=0 NormalX=0 NormalY=0 NormalZ=1 AngleXU=0 Radius=1
    g173: Circle CenterX=179.022 CenterY=124.221 CenterZ=0 NormalX=0 NormalY=0 NormalZ=1 AngleXU=0 Radius=1
    g174: Circle CenterX=179.022 CenterY=120.221 CenterZ=0 NormalX=0 NormalY=0 NormalZ=1 AngleXU=0 Radius=1
    g175: BSplineCurve PolesCount=3 KnotsCount=2 Degree=2 IsPeriodic=0
    g176: GeomPoint X=175.022 Y=124.221 Z=0
    g177: GeomPoint X=179.022 Y=120.221 Z=0
    g178: Circle CenterX=62.0728 CenterY=124.221 CenterZ=0 NormalX=0 NormalY=0 NormalZ=1 AngleXU=0 Radius=1
    g179: Circle CenterX=58.0728 CenterY=124.221 CenterZ=0 NormalX=0 NormalY=0 NormalZ=1 AngleXU=0 Radius=1
    g180: Circle CenterX=61.1496 CenterY=121.665 CenterZ=0 NormalX=0 NormalY=0 NormalZ=1 AngleXU=0 Radius=1
    g181: BSplineCurve PolesCount=3 KnotsCount=2 Degree=2 IsPeriodic=0
    g182: GeomPoint X=62.0728 Y=124.221 Z=0
    g183: GeomPoint X=61.1496 Y=121.665 Z=0
    g184: LineSegment StartX=62.0728 StartY=124.221 StartZ=0 EndX=175.022 EndY=124.221 EndZ=0
    g185: LineSegment StartX=179.022 StartY=120.221 StartZ=0 EndX=179.022 EndY=27.0628 EndZ=0
    g186: LineSegment StartX=185.124 StartY=27.0628 StartZ=0 EndX=185.124 EndY=120.221 EndZ=0
    g187: LineSegment StartX=189.124 StartY=124.221 StartZ=0 EndX=302.073 EndY=124.221 EndZ=0
    g188: LineSegment StartX=302.996 StartY=121.665 StartZ=0 EndX=189.124 EndY=27.0628 EndZ=0
    g189: LineSegment StartX=175.022 StartY=27.0628 StartZ=0 EndX=61.1496 EndY=121.665 EndZ=0
    g190: Circle CenterX=61.5791 CenterY=75.4095 CenterZ=0 NormalX=0 NormalY=0 NormalZ=1 AngleXU=0 Radius=1
    g191: Circle CenterX=58.0728 CenterY=77.3346 CenterZ=0 NormalX=0 NormalY=0 NormalZ=1 AngleXU=0 Radius=1
    g192: Circle CenterX=58.0728 CenterY=73.3346 CenterZ=0 NormalX=0 NormalY=0 NormalZ=1 AngleXU=0 Radius=1
    g193: BSplineCurve PolesCount=3 KnotsCount=2 Degree=2 IsPeriodic=0
    g194: GeomPoint X=61.5791 Y=75.4095 Z=0
    g195: GeomPoint X=58.0728 Y=73.3346 Z=0
    g196: Circle CenterX=58.0728 CenterY=-40.8935 CenterZ=0 NormalX=0 NormalY=0 NormalZ=1 AngleXU=0 Radius=1
    g197: Circle CenterX=58.0728 CenterY=-44.8935 CenterZ=0 NormalX=0 NormalY=0 NormalZ=1 AngleXU=0 Radius=1
    g198: Circle CenterX=61.5791 CenterY=-42.9683 CenterZ=0 NormalX=0 NormalY=0 NormalZ=1 AngleXU=0 Radius=1
    g199: BSplineCurve PolesCount=3 KnotsCount=2 Degree=2 IsPeriodic=0
    g200: GeomPoint X=58.0728 Y=-40.8935 Z=0
    g201: GeomPoint X=61.5791 Y=-42.9683 Z=0
    g202: LineSegment StartX=61.5791 StartY=-42.9683 StartZ=0 EndX=165.871 EndY=14.2954 EndZ=0
    g203: LineSegment StartX=165.871 StartY=18.1458 StartZ=0 EndX=61.5791 EndY=75.4095 EndZ=0
    g204: LineSegment StartX=58.0728 StartY=73.3346 StartZ=0 EndX=58.0728 EndY=-40.8935 EndZ=0
    g205: Circle CenterX=302.567 CenterY=-42.9683 CenterZ=0 NormalX=0 NormalY=0 NormalZ=1 AngleXU=0 Radius=1
    g206: Circle CenterX=306.073 CenterY=-44.8935 CenterZ=0 NormalX=0 NormalY=0 NormalZ=1 AngleXU=0 Radius=1
    g207: Circle CenterX=306.073 CenterY=-40.8935 CenterZ=0 NormalX=0 NormalY=0 NormalZ=1 AngleXU=0 Radius=1
    g208: BSplineCurve PolesCount=3 KnotsCount=2 Degree=2 IsPeriodic=0
    g209: GeomPoint X=302.567 Y=-42.9683 Z=0
    g210: GeomPoint X=306.073 Y=-40.8935 Z=0
    g211: Circle CenterX=306.073 CenterY=73.3346 CenterZ=0 NormalX=0 NormalY=0 NormalZ=1 AngleXU=0 Radius=1
    g212: Circle CenterX=306.073 CenterY=77.3346 CenterZ=0 NormalX=0 NormalY=0 NormalZ=1 AngleXU=0 Radius=1
    g213: Circle CenterX=302.567 CenterY=75.4095 CenterZ=0 NormalX=0 NormalY=0 NormalZ=1 AngleXU=0 Radius=1
    g214: BSplineCurve PolesCount=3 KnotsCount=2 Degree=2 IsPeriodic=0
    g215: GeomPoint X=306.073 Y=73.3346 Z=0
    g216: GeomPoint X=302.567 Y=75.4095 Z=0
    g217: LineSegment StartX=302.567 StartY=-42.9683 StartZ=0 EndX=198.275 EndY=14.2954 EndZ=0
    g218: LineSegment StartX=198.275 StartY=18.1458 StartZ=0 EndX=302.567 EndY=75.4095 EndZ=0
    g219: LineSegment StartX=306.073 StartY=73.3346 StartZ=0 EndX=306.073 EndY=-40.8935 EndZ=0
    g220: LineSegment StartX=322.073 StartY=105.865 StartZ=0 EndX=328.643 EndY=105.865 EndZ=0
    g221: LineSegment StartX=318.073 StartY=120.221 StartZ=0 EndX=318.073 EndY=109.865 EndZ=0
    g222: LineSegment StartX=336.157 StartY=107.779 StartZ=0 EndX=362.567 EndY=122.294 EndZ=0
    g223: Circle CenterX=362.073 CenterY=124.221 CenterZ=0 NormalX=0 NormalY=0 NormalZ=1 AngleXU=0 Radius=1
    g224: Circle CenterX=366.073 CenterY=124.221 CenterZ=0 NormalX=0 NormalY=0 NormalZ=1 AngleXU=0 Radius=1
    g225: Circle CenterX=362.567 CenterY=122.294 CenterZ=0 NormalX=0 NormalY=0 NormalZ=1 AngleXU=0 Radius=1
    g226: BSplineCurve PolesCount=3 KnotsCount=2 Degree=2 IsPeriodic=0
    g227: GeomPoint X=362.073 Y=124.221 Z=0
    g228: GeomPoint X=362.567 Y=122.294 Z=0
    g229: Circle CenterX=322.073 CenterY=124.221 CenterZ=0 NormalX=0 NormalY=0 NormalZ=1 AngleXU=0 Radius=1
    g230: Circle CenterX=318.073 CenterY=124.221 CenterZ=0 NormalX=0 NormalY=0 NormalZ=1 AngleXU=0 Radius=1
    g231: Circle CenterX=318.073 CenterY=120.221 CenterZ=0 NormalX=0 NormalY=0 NormalZ=1 AngleXU=0 Radius=1
    g232: BSplineCurve PolesCount=3 KnotsCount=2 Degree=2 IsPeriodic=0
    g233: GeomPoint X=322.073 Y=124.221 Z=0
    g234: GeomPoint X=318.073 Y=120.221 Z=0
    g235: Circle CenterX=322.073 CenterY=105.865 CenterZ=0 NormalX=0 NormalY=0 NormalZ=1 AngleXU=0 Radius=1
    g236: Circle CenterX=318.073 CenterY=105.865 CenterZ=0 NormalX=0 NormalY=0 NormalZ=1 AngleXU=0 Radius=1
    g237: Circle CenterX=318.073 CenterY=109.865 CenterZ=0 NormalX=0 NormalY=0 NormalZ=1 AngleXU=0 Radius=1
    g238: BSplineCurve PolesCount=3 KnotsCount=2 Degree=2 IsPeriodic=0
    g239: GeomPoint X=322.073 Y=105.865 Z=0
    g240: GeomPoint X=318.073 Y=109.865 Z=0
    g241: Circle CenterX=336.157 CenterY=107.779 CenterZ=0 NormalX=0 NormalY=0 NormalZ=1 AngleXU=0 Radius=1
    g242: Circle CenterX=332.651 CenterY=105.853 CenterZ=0 NormalX=0 NormalY=0 NormalZ=1 AngleXU=0 Radius=1
    g243: Circle CenterX=328.643 CenterY=105.865 CenterZ=0 NormalX=0 NormalY=0 NormalZ=1 AngleXU=0 Radius=1
    g244: BSplineCurve PolesCount=3 KnotsCount=2 Degree=2 IsPeriodic=0
    g245: GeomPoint X=336.157 Y=107.779 Z=0
    g246: GeomPoint X=328.643 Y=105.865 Z=0
    g247: LineSegment StartX=322.073 StartY=124.221 StartZ=0 EndX=362.073 EndY=124.221 EndZ=0
    g248: Circle CenterX=371.567 CenterY=-80.8644 CenterZ=0 NormalX=0 NormalY=0 NormalZ=1 AngleXU=0 Radius=1
    g249: Circle CenterX=375.073 CenterY=-82.7896 CenterZ=0 NormalX=0 NormalY=0 NormalZ=1 AngleXU=0 Radius=1
    g250: Circle CenterX=375.073 CenterY=-78.7896 CenterZ=0 NormalX=0 NormalY=0 NormalZ=1 AngleXU=0 Radius=1
    g251: BSplineCurve PolesCount=3 KnotsCount=2 Degree=2 IsPeriodic=0
    g252: GeomPoint X=371.567 Y=-80.8644 Z=0
    g253: GeomPoint X=375.073 Y=-78.7896 Z=0
    g254: Circle CenterX=321.579 CenterY=-53.4075 CenterZ=0 NormalX=0 NormalY=0 NormalZ=1 AngleXU=0 Radius=1
    g255: Circle CenterX=318.073 CenterY=-51.4823 CenterZ=0 NormalX=0 NormalY=0 NormalZ=1 AngleXU=0 Radius=1
    g256: Circle CenterX=318.073 CenterY=-47.4805 CenterZ=0 NormalX=0 NormalY=0 NormalZ=1 AngleXU=0 Radius=1
    g257: BSplineCurve PolesCount=3 KnotsCount=2 Degree=2 IsPeriodic=0
    g258: GeomPoint X=321.579 Y=-53.4075 Z=0
    g259: GeomPoint X=318.073 Y=-47.4805 Z=0
    g260: LineSegment StartX=371.567 StartY=-80.8644 StartZ=0 EndX=321.579 EndY=-53.4075 EndZ=0
    g261: Circle CenterX=321.579 CenterY=-67.3492 CenterZ=0 NormalX=0 NormalY=0 NormalZ=1 AngleXU=0 Radius=1
    g262: Circle CenterX=318.073 CenterY=-65.424 CenterZ=0 NormalX=0 NormalY=0 NormalZ=1 AngleXU=0 Radius=1
    g263: Circle CenterX=318.073 CenterY=-69.424 CenterZ=0 NormalX=0 NormalY=0 NormalZ=1 AngleXU=0 Radius=1
    g264: BSplineCurve PolesCount=3 KnotsCount=2 Degree=2 IsPeriodic=0
    g265: GeomPoint X=321.579 Y=-67.3492 Z=0
    g266: GeomPoint X=318.073 Y=-69.424 Z=0
    g267: Circle CenterX=362.567 CenterY=-89.8542 CenterZ=0 NormalX=0 NormalY=0 NormalZ=1 AngleXU=0 Radius=1
    g268: Circle CenterX=366.073 CenterY=-91.7794 CenterZ=0 NormalX=0 NormalY=0 NormalZ=1 AngleXU=0 Radius=1
    g269: Circle CenterX=362.073 CenterY=-91.7794 CenterZ=0 NormalX=0 NormalY=0 NormalZ=1 AngleXU=0 Radius=1
    g270: BSplineCurve PolesCount=3 KnotsCount=2 Degree=2 IsPeriodic=0
    g271: GeomPoint X=362.567 Y=-89.8542 Z=0
    g272: GeomPoint X=362.073 Y=-91.7794 Z=0
    g273: Circle CenterX=322.073 CenterY=-91.7794 CenterZ=0 NormalX=0 NormalY=0 NormalZ=1 AngleXU=0 Radius=1
    g274: Circle CenterX=318.073 CenterY=-91.7794 CenterZ=0 NormalX=0 NormalY=0 NormalZ=1 AngleXU=0 Radius=1
    g275: Circle CenterX=318.073 CenterY=-87.7794 CenterZ=0 NormalX=0 NormalY=0 NormalZ=1 AngleXU=0 Radius=1
    g276: BSplineCurve PolesCount=3 KnotsCount=2 Degree=2 IsPeriodic=0
    g277: GeomPoint X=322.073 Y=-91.7794 Z=0
    g278: GeomPoint X=318.073 Y=-87.7794 Z=0
    g279: LineSegment StartX=362.567 StartY=-89.8542 StartZ=0 EndX=321.579 EndY=-67.3492 EndZ=0
    g280: LineSegment StartX=318.073 StartY=-69.424 StartZ=0 EndX=318.073 EndY=-87.7794 EndZ=0
    g281: LineSegment StartX=322.073 StartY=-91.7794 StartZ=0 EndX=362.073 EndY=-91.7794 EndZ=0
    g282: Circle CenterX=2.07281 CenterY=124.221 CenterZ=0 NormalX=0 NormalY=0 NormalZ=1 AngleXU=0 Radius=1
    g283: Circle CenterX=1.57905 CenterY=122.295 CenterZ=0 NormalX=0 NormalY=0 NormalZ=1 AngleXU=0 Radius=1
    g284: BSplineCurve PolesCount=3 KnotsCount=2 Degree=2 IsPeriodic=0
    g285: GeomPoint X=2.07281 Y=124.221 Z=0
    g286: GeomPoint X=1.57905 Y=122.295 Z=0
    g287: Circle CenterX=42.0728 CenterY=124.221 CenterZ=0 NormalX=0 NormalY=0 NormalZ=1 AngleXU=0 Radius=1
    g288: Circle CenterX=46.0728 CenterY=124.221 CenterZ=0 NormalX=0 NormalY=0 NormalZ=1 AngleXU=0 Radius=1
    g289: Circle CenterX=46.0728 CenterY=120.221 CenterZ=0 NormalX=0 NormalY=0 NormalZ=1 AngleXU=0 Radius=1
    g290: BSplineCurve PolesCount=3 KnotsCount=2 Degree=2 IsPeriodic=0
    g291: GeomPoint X=42.0728 Y=124.221 Z=0
    g292: GeomPoint X=46.0728 Y=120.221 Z=0
    g293: Circle CenterX=46.0728 CenterY=109.865 CenterZ=0 NormalX=0 NormalY=0 NormalZ=1 AngleXU=0 Radius=1
    g294: Circle CenterX=46.0728 CenterY=105.865 CenterZ=0 NormalX=0 NormalY=0 NormalZ=1 AngleXU=0 Radius=1
    g295: Circle CenterX=42.0728 CenterY=105.865 CenterZ=0 NormalX=0 NormalY=0 NormalZ=1 AngleXU=0 Radius=1
    g296: BSplineCurve PolesCount=3 KnotsCount=2 Degree=2 IsPeriodic=0
    g297: GeomPoint X=46.0728 Y=109.865 Z=0
    g298: GeomPoint X=42.0728 Y=105.865 Z=0
    g299: Circle CenterX=35.5028 CenterY=105.865 CenterZ=0 NormalX=0 NormalY=0 NormalZ=1 AngleXU=0 Radius=1
    g300: Circle CenterX=31.5028 CenterY=105.865 CenterZ=0 NormalX=0 NormalY=0 NormalZ=1 AngleXU=0 Radius=1
    g301: Circle CenterX=27.9965 CenterY=107.79 CenterZ=0 NormalX=0 NormalY=0 NormalZ=1 AngleXU=0 Radius=1
    g302: BSplineCurve PolesCount=3 KnotsCount=2 Degree=2 IsPeriodic=0
    g303: GeomPoint X=35.5028 Y=105.865 Z=0
    g304: GeomPoint X=27.9965 Y=107.79 Z=0
    g305: LineSegment StartX=2.07281 StartY=124.221 StartZ=0 EndX=42.0728 EndY=124.221 EndZ=0
    g306: LineSegment StartX=46.0728 StartY=120.221 StartZ=0 EndX=46.0728 EndY=109.865 EndZ=0
    g307: LineSegment StartX=42.0728 StartY=105.865 StartZ=0 EndX=35.5028 EndY=105.865 EndZ=0
    g308: LineSegment StartX=27.9965 StartY=107.79 StartZ=0 EndX=1.57905 EndY=122.295 EndZ=0
    g309: Circle CenterX=42.5666 CenterY=-67.3492 CenterZ=0 NormalX=0 NormalY=0 NormalZ=1 AngleXU=0 Radius=1
    g310: Circle CenterX=46.0728 CenterY=-65.424 CenterZ=0 NormalX=0 NormalY=0 NormalZ=1 AngleXU=0 Radius=1
    g311: Circle CenterX=46.0728 CenterY=-69.424 CenterZ=0 NormalX=0 NormalY=0 NormalZ=1 AngleXU=0 Radius=1
    g312: BSplineCurve PolesCount=3 KnotsCount=2 Degree=2 IsPeriodic=0
    g313: GeomPoint X=42.5666 Y=-67.3492 Z=0
    g314: GeomPoint X=46.0728 Y=-69.424 Z=0
    g315: Circle CenterX=46.0728 CenterY=-87.7794 CenterZ=0 NormalX=0 NormalY=0 NormalZ=1 AngleXU=0 Radius=1
    g316: Circle CenterX=46.0728 CenterY=-91.7794 CenterZ=0 NormalX=0 NormalY=0 NormalZ=1 AngleXU=0 Radius=1
    g317: Circle CenterX=42.0728 CenterY=-91.7794 CenterZ=0 NormalX=0 NormalY=0 NormalZ=1 AngleXU=0 Radius=1
    g318: BSplineCurve PolesCount=3 KnotsCount=2 Degree=2 IsPeriodic=0
    g319: GeomPoint X=46.0728 Y=-87.7794 Z=0
    g320: GeomPoint X=42.0728 Y=-91.7794 Z=0
    g321: Circle CenterX=2.07281 CenterY=-91.7794 CenterZ=0 NormalX=0 NormalY=0 NormalZ=1 AngleXU=0 Radius=1
    g322: Circle CenterX=-1.92719 CenterY=-91.7794 CenterZ=0 NormalX=0 NormalY=0 NormalZ=1 AngleXU=0 Radius=1
    g323: Circle CenterX=1.57905 CenterY=-89.8542 CenterZ=0 NormalX=0 NormalY=0 NormalZ=1 AngleXU=0 Radius=1
    g324: BSplineCurve PolesCount=3 KnotsCount=2 Degree=2 IsPeriodic=0
    g325: GeomPoint X=2.07281 Y=-91.7794 Z=0
    g326: GeomPoint X=1.57905 Y=-89.8542 Z=0
    g327: LineSegment StartX=2.07281 StartY=-91.7794 StartZ=0 EndX=42.0728 EndY=-91.7794 EndZ=0
    g328: LineSegment StartX=46.0728 StartY=-87.7794 StartZ=0 EndX=46.0728 EndY=-69.424 EndZ=0
    g329: LineSegment StartX=42.5666 StartY=-67.3492 StartZ=0 EndX=1.57905 EndY=-89.8542 EndZ=0
    g330: Circle CenterX=322.073 CenterY=76.4095 CenterZ=0 NormalX=0 NormalY=0 NormalZ=1 AngleXU=0 Radius=4
    g331: BSplineCurve PolesCount=3 KnotsCount=2 Degree=2 IsPeriodic=0
    g332: GeomPoint X=318.073 Y=72.4095 Z=0
    g333: GeomPoint X=322.073 Y=76.4095 Z=0
    g334: Circle CenterX=375.073 CenterY=72.4095 CenterZ=0 NormalX=0 NormalY=0 NormalZ=1 AngleXU=0 Radius=1
    g335: Circle CenterX=375.073 CenterY=76.4095 CenterZ=0 NormalX=0 NormalY=0 NormalZ=1 AngleXU=0 Radius=1
    g336: Circle CenterX=371.073 CenterY=76.4095 CenterZ=0 NormalX=0 NormalY=0 NormalZ=1 AngleXU=0 Radius=1
    g337: BSplineCurve PolesCount=3 KnotsCount=2 Degree=2 IsPeriodic=0
    g338: GeomPoint X=375.073 Y=72.4095 Z=0
    g339: GeomPoint X=371.073 Y=76.4095 Z=0
    g340: LineSegment StartX=322.073 StartY=76.4095 StartZ=0 EndX=371.073 EndY=76.4095 EndZ=0
    g341: LineSegment StartX=318.073 StartY=72.4095 StartZ=0 EndX=318.073 EndY=-47.4805 EndZ=0
    g342: LineSegment StartX=375.073 StartY=72.4095 StartZ=0 EndX=375.073 EndY=-78.7896 EndZ=0
    g343: ArcOfCircle CenterX=-26.9272 CenterY=22.1087 CenterZ=0 NormalX=0 NormalY=0 NormalZ=1 AngleXU=0 Radius=4 StartAngle=5e-16 EndAngle=3.14159
    g344: LineSegment StartX=-22.9272 StartY=22.1087 StartZ=0 EndX=-18.9272 EndY=-83.7794 EndZ=0
    g345: LineSegment StartX=-34.9272 StartY=-83.7794 StartZ=0 EndX=-30.9272 EndY=22.1087 EndZ=0
    g346: ArcOfCircle CenterX=391.073 CenterY=22.1087 CenterZ=0 NormalX=0 NormalY=0 NormalZ=1 AngleXU=0 Radius=4 StartAngle=0 EndAngle=3.14159
    g347: LineSegment StartX=387.073 StartY=22.1087 StartZ=0 EndX=383.073 EndY=-83.7794 EndZ=0
    g348: LineSegment StartX=395.073 StartY=22.1087 StartZ=0 EndX=399.073 EndY=-83.7794 EndZ=0
  constraints (573):
    c: Coincident(g0,g2)
    c: Block(g0)
    c: Block(g1)
    c: Vertical(g3)
    c: Vertical(g4)
    c: Block(g4)
    c: Block(g3)
    c: Weight(g7) = 1
    c: Equal(g7,g8)
    c: Equal(g7,g9)
    c: InternalAlignment(g7,g10)
    c: InternalAlignment(g8,g10)
    c: InternalAlignment(g9,g10)
    c: InternalAlignment(g11,g10)
    c: InternalAlignment(g12,g10)
    c: Weight(g13) = 1
    c: Equal(g13,g14)
    c: Equal(g13,g15)
    c: InternalAlignment(g13,g16)
    c: InternalAlignment(g14,g16)
    c: InternalAlignment(g15,g16)
    c: InternalAlignment(g17,g16)
    c: InternalAlignment(g18,g16)
    c: Block(g16)
    c: Block(g10)
    c: Weight(g19) = 1
    c: Equal(g19,g20)
    c: Equal(g19,g21)
    c: InternalAlignment(g19,g22)
    c: InternalAlignment(g20,g22)
    c: InternalAlignment(g21,g22)
    c: InternalAlignment(g23,g22)
    c: InternalAlignment(g24,g22)
    c: Weight(g25) = 1
    c: Equal(g25,g26)
    c: Equal(g25,g27)
    c: InternalAlignment(g25,g28)
    c: InternalAlignment(g26,g28)
    c: InternalAlignment(g27,g28)
    c: InternalAlignment(g29,g28)
    c: InternalAlignment(g30,g28)
    c: Block(g28)
    c: Block(g22)
    c: Weight(g31) = 1
    c: Equal(g31,g32)
    c: Equal(g31,g33)
    c: InternalAlignment(g31,g34)
    c: InternalAlignment(g32,g34)
    c: InternalAlignment(g33,g34)
    c: InternalAlignment(g35,g34)
    c: InternalAlignment(g36,g34)
    c: Weight(g37) = 1
    c: Equal(g37,g38)
    c: Equal(g37,g39)
    c: InternalAlignment(g37,g40)
    c: InternalAlignment(g38,g40)
    c: InternalAlignment(g39,g40)
    c: InternalAlignment(g41,g40)
    c: InternalAlignment(g42,g40)
    c: Block(g34)
    c: Block(g40)
    c: Coincident(g43,g4)
    c: Coincident(g43,g3)
    c: Horizontal(g43)
    c: Distance(g43) = 450
    c: Coincident(g44,g4)
    c: Coincident(g44,g3)
    c: Horizontal(g44)
    c: Horizontal(g45)
    c: Coincident(g2,g45)
    c: Block(g45)
    c: Coincident(g1,g45)
    c: Weight(g46) = 1
    c: Equal(g46,g47)
    c: Equal(g46,g48)
    c: InternalAlignment(g46,g49)
    c: InternalAlignment(g47,g49)
    c: InternalAlignment(g48,g49)
    c: InternalAlignment(g50,g49)
    c: InternalAlignment(g51,g49)
    c: Block(g49)
    c: Weight(g52) = 1
    c: Equal(g52,g53)
    c: Equal(g52,g54)
    c: InternalAlignment(g52,g55)
    c: InternalAlignment(g53,g55)
    c: InternalAlignment(g54,g55)
    c: InternalAlignment(g56,g55)
    c: InternalAlignment(g57,g55)
    c: Block(g55)
    c: Weight(g58) = 1
    c: Equal(g58,g59)
    c: Equal(g58,g60)
    c: InternalAlignment(g58,g61)
    c: InternalAlignment(g59,g61)
    c: InternalAlignment(g60,g61)
    c: InternalAlignment(g62,g61)
    c: InternalAlignment(g63,g61)
    c: Block(g61)
    c: Weight(g64) = 1
    c: Equal(g64,g65)
    c: Equal(g64,g66)
    c: InternalAlignment(g64,g67)
    c: InternalAlignment(g65,g67)
    c: InternalAlignment(g66,g67)
    c: InternalAlignment(g68,g67)
    c: InternalAlignment(g69,g67)
    c: Block(g67)
    c: Weight(g70) = 1
    c: Equal(g70,g71)
    c: Equal(g70,g72)
    c: InternalAlignment(g70,g73)
    c: InternalAlignment(g71,g73)
    c: InternalAlignment(g72,g73)
    c: InternalAlignment(g74,g73)
    c: InternalAlignment(g75,g73)
    c: Weight(g76) = 1
    c: Equal(g76,g77)
    c: Equal(g76,g78)
    c: InternalAlignment(g76,g79)
    c: InternalAlignment(g77,g79)
    c: InternalAlignment(g78,g79)
    c: InternalAlignment(g80,g79)
    c: InternalAlignment(g81,g79)
    c: Block(g73)
    c: Block(g79)
    c: Coincident(g82,g73)
    c: Coincident(g82,g79)
    c: Vertical(g82)
    c: Coincident(g83,g73)
    c: Coincident(g83,g55)
    c: Coincident(g84,g55)
    c: Coincident(g84,g79)
    c: Weight(g85) = 1
    c: Equal(g85,g86)
    c: Equal(g85,g87)
    c: InternalAlignment(g85,g88)
    c: InternalAlignment(g86,g88)
    c: InternalAlignment(g87,g88)
    c: InternalAlignment(g89,g88)
    c: InternalAlignment(g90,g88)
    c: Weight(g91) = 1
    c: Equal(g91,g92)
    c: Equal(g91,g93)
    c: InternalAlignment(g91,g94)
    c: InternalAlignment(g92,g94)
    c: InternalAlignment(g93,g94)
    c: InternalAlignment(g95,g94)
    c: InternalAlignment(g96,g94)
    c: Block(g88)
    c: Block(g94)
    c: Coincident(g97,g88)
    c: Coincident(g97,g94)
    c: Vertical(g97)
    c: Coincident(g98,g88)
    c: Coincident(g98,g49)
    c: Coincident(g99,g49)
    c: Coincident(g99,g94)
    c: Weight(g100) = 1
    c: Equal(g100,g101)
    c: Equal(g100,g102)
    c: InternalAlignment(g100,g103)
    c: InternalAlignment(g101,g103)
    c: InternalAlignment(g102,g103)
    c: InternalAlignment(g104,g103)
    c: InternalAlignment(g105,g103)
    c: Weight(g106) = 1
    c: Equal(g106,g107)
    c: Equal(g106,g108)
    c: InternalAlignment(g106,g109)
    c: InternalAlignment(g107,g109)
    c: InternalAlignment(g108,g109)
    c: InternalAlignment(g110,g109)
    c: InternalAlignment(g111,g109)
    c: Block(g103)
    c: Block(g109)
    c: Coincident(g112,g103)
    c: Coincident(g112,g109)
    c: Vertical(g112)
    c: Coincident(g113,g109)
    c: Coincident(g113,g67)
    c: Coincident(g114,g67)
    c: Coincident(g114,g103)
    c: Weight(g115) = 1
    c: Equal(g115,g116)
    c: Equal(g115,g117)
    c: InternalAlignment(g115,g118)
    c: InternalAlignment(g116,g118)
    c: InternalAlignment(g117,g118)
    c: InternalAlignment(g119,g118)
    c: InternalAlignment(g120,g118)
    c: Weight(g121) = 1
    c: Equal(g121,g122)
    c: Equal(g121,g123)
    c: InternalAlignment(g121,g124)
    c: InternalAlignment(g122,g124)
    c: InternalAlignment(g123,g124)
    c: InternalAlignment(g125,g124)
    c: InternalAlignment(g126,g124)
    c: Block(g118)
    c: Block(g124)
    c: Coincident(g127,g118)
    c: Coincident(g127,g124)
    c: Vertical(g127)
    c: Coincident(g128,g124)
    c: Coincident(g128,g61)
    c: Coincident(g129,g61)
    c: Coincident(g129,g118)
    c: Weight(g130) = 1
    c: Equal(g130,g131)
    c: Equal(g130,g132)
    c: InternalAlignment(g130,g133)
    c: InternalAlignment(g131,g133)
    c: InternalAlignment(g132,g133)
    c: InternalAlignment(g134,g133)
    c: InternalAlignment(g135,g133)
    c: Weight(g136) = 1
    c: Equal(g136,g137)
    c: Equal(g136,g138)
    c: InternalAlignment(g136,g139)
    c: InternalAlignment(g137,g139)
    c: InternalAlignment(g138,g139)
    c: InternalAlignment(g140,g139)
    c: InternalAlignment(g141,g139)
    c: Weight(g142) = 1
    c: Equal(g142,g143)
    c: Equal(g142,g144)
    c: InternalAlignment(g142,g145)
    c: InternalAlignment(g143,g145)
    c: InternalAlignment(g144,g145)
    c: InternalAlignment(g146,g145)
    c: InternalAlignment(g147,g145)
    c: Weight(g148) = 1
    c: Equal(g148,g149)
    c: Equal(g148,g150)
    c: InternalAlignment(g148,g151)
    c: InternalAlignment(g149,g151)
    c: InternalAlignment(g150,g151)
    c: InternalAlignment(g152,g151)
    c: InternalAlignment(g153,g151)
    c: Block(g151)
    c: Block(g145)
    c: Block(g139)
    c: Block(g133)
    c: Coincident(g154,g28)
    c: Coincident(g154,g151)
    c: Coincident(g155,g151)
    c: Coincident(g155,g145)
    c: Horizontal(g155)
    c: Coincident(g156,g145)
    c: Coincident(g156,g28)
    c: Vertical(g156)
    c: Coincident(g157,g22)
    c: Coincident(g157,g139)
    c: Vertical(g157)
    c: Coincident(g158,g139)
    c: Coincident(g158,g133)
    c: Horizontal(g158)
    c: Coincident(g159,g133)
    c: Coincident(g159,g22)
    c: Weight(g160) = 1
    c: Equal(g160,g161)
    c: Equal(g160,g162)
    c: InternalAlignment(g160,g163)
    c: InternalAlignment(g161,g163)
    c: InternalAlignment(g162,g163)
    c: InternalAlignment(g164,g163)
    c: InternalAlignment(g165,g163)
    c: Weight(g166) = 1
    c: Equal(g166,g167)
    c: Equal(g166,g168)
    c: InternalAlignment(g166,g169)
    c: InternalAlignment(g167,g169)
    c: InternalAlignment(g168,g169)
    c: InternalAlignment(g170,g169)
    c: InternalAlignment(g171,g169)
    c: Weight(g172) = 1
    c: Equal(g172,g173)
    c: Equal(g172,g174)
    c: InternalAlignment(g172,g175)
    c: InternalAlignment(g173,g175)
    c: InternalAlignment(g174,g175)
    c: InternalAlignment(g176,g175)
    c: InternalAlignment(g177,g175)
    c: Weight(g178) = 1
    c: Equal(g178,g179)
    c: Equal(g178,g180)
    c: InternalAlignment(g178,g181)
    c: InternalAlignment(g179,g181)
    c: InternalAlignment(g180,g181)
    c: InternalAlignment(g182,g181)
    c: InternalAlignment(g183,g181)
    c: Block(g181)
    c: Block(g175)
    c: Block(g169)
    c: Block(g163)
    c: Coincident(g184,g181)
    c: Coincident(g184,g175)
    c: Horizontal(g184)
    c: Coincident(g185,g175)
    c: Coincident(g185,g10)
    c: Vertical(g185)
    c: Coincident(g186,g16)
    c: Coincident(g186,g169)
    c: Vertical(g186)
    c: Coincident(g187,g169)
    c: Coincident(g187,g163)
    c: Horizontal(g187)
    c: Coincident(g188,g163)
    c: Coincident(g188,g16)
    c: Coincident(g189,g10)
    c: Weight(g190) = 1
    c: Equal(g190,g191)
    c: Equal(g190,g192)
    c: InternalAlignment(g190,g193)
    c: InternalAlignment(g191,g193)
    c: InternalAlignment(g192,g193)
    c: InternalAlignment(g194,g193)
    c: InternalAlignment(g195,g193)
    c: Weight(g196) = 1
    c: Equal(g196,g197)
    c: Equal(g196,g198)
    c: InternalAlignment(g196,g199)
    c: InternalAlignment(g197,g199)
    c: InternalAlignment(g198,g199)
    c: InternalAlignment(g200,g199)
    c: InternalAlignment(g201,g199)
    c: Block(g199)
    c: Block(g193)
    c: Coincident(g202,g199)
    c: Coincident(g202,g34)
    c: Coincident(g203,g34)
    c: Coincident(g203,g193)
    c: Coincident(g204,g193)
    c: Coincident(g204,g199)
    c: Vertical(g204)
    c: Weight(g205) = 1
    c: Equal(g205,g206)
    c: Equal(g205,g207)
    c: InternalAlignment(g205,g208)
    c: InternalAlignment(g206,g208)
    c: InternalAlignment(g207,g208)
    c: InternalAlignment(g209,g208)
    c: InternalAlignment(g210,g208)
    c: Weight(g211) = 1
    c: Equal(g211,g212)
    c: Equal(g211,g213)
    c: InternalAlignment(g211,g214)
    c: InternalAlignment(g212,g214)
    c: InternalAlignment(g213,g214)
    c: InternalAlignment(g215,g214)
    c: InternalAlignment(g216,g214)
    c: Block(g214)
    c: Block(g208)
    c: Coincident(g217,g208)
    c: Coincident(g217,g40)
    c: Coincident(g218,g40)
    c: Coincident(g218,g214)
    c: Coincident(g219,g214)
    c: Coincident(g219,g208)
    c: Vertical(g219)
    c: Horizontal(g220)
    c: Block(g220)
    c: Vertical(g221)
    c: Block(g221)
    c: Block(g222)
    c: Weight(g223) = 1
    c: Equal(g223,g224)
    c: Equal(g223,g225)
    c: InternalAlignment(g223,g226)
    c: InternalAlignment(g224,g226)
    c: InternalAlignment(g225,g226)
    c: InternalAlignment(g227,g226)
    c: InternalAlignment(g228,g226)
    c: Weight(g229) = 1
    c: Equal(g229,g230)
    c: Equal(g229,g231)
    c: InternalAlignment(g229,g232)
    c: InternalAlignment(g230,g232)
    c: InternalAlignment(g231,g232)
    c: InternalAlignment(g233,g232)
    c: InternalAlignment(g234,g232)
    c: Weight(g235) = 1
    c: Equal(g235,g236)
    c: Equal(g235,g237)
    c: InternalAlignment(g235,g238)
    c: InternalAlignment(g236,g238)
    c: InternalAlignment(g237,g238)
    c: InternalAlignment(g239,g238)
    c: InternalAlignment(g240,g238)
    c: Weight(g241) = 1
    c: Equal(g241,g242)
    c: Equal(g241,g243)
    c: InternalAlignment(g241,g244)
    c: InternalAlignment(g242,g244)
    c: InternalAlignment(g243,g244)
    c: InternalAlignment(g245,g244)
    c: InternalAlignment(g246,g244)
    c: Block(g226)
    c: Block(g232)
    c: Block(g238)
    c: Block(g244)
    c: Coincident(g247,g232)
    c: Coincident(g247,g226)
    c: Horizontal(g247)
    c: Block(g189)
    c: Weight(g248) = 1
    c: Equal(g248,g249)
    c: Equal(g248,g250)
    c: InternalAlignment(g248,g251)
    c: InternalAlignment(g249,g251)
    c: InternalAlignment(g250,g251)
    c: InternalAlignment(g252,g251)
    c: InternalAlignment(g253,g251)
    c: Weight(g254) = 1
    c: Equal(g254,g255)
    c: Equal(g254,g256)
    c: InternalAlignment(g254,g257)
    c: InternalAlignment(g255,g257)
    c: InternalAlignment(g256,g257)
    c: InternalAlignment(g258,g257)
    c: InternalAlignment(g259,g257)
    c: Block(g251)
    c: Block(g257)
    c: Coincident(g260,g251)
    c: Coincident(g260,g257)
    c: Weight(g261) = 1
    c: Equal(g261,g262)
    c: Equal(g261,g263)
    c: InternalAlignment(g261,g264)
    c: InternalAlignment(g262,g264)
    c: InternalAlignment(g263,g264)
    c: InternalAlignment(g265,g264)
    c: InternalAlignment(g266,g264)
    c: Weight(g267) = 1
    c: Equal(g267,g268)
    c: Equal(g267,g269)
    c: InternalAlignment(g267,g270)
    c: InternalAlignment(g268,g270)
    c: InternalAlignment(g269,g270)
    c: InternalAlignment(g271,g270)
    c: InternalAlignment(g272,g270)
    c: Weight(g273) = 1
    c: Equal(g273,g274)
    c: Equal(g273,g275)
    c: InternalAlignment(g273,g276)
    c: InternalAlignment(g274,g276)
    c: InternalAlignment(g275,g276)
    c: InternalAlignment(g277,g276)
    c: InternalAlignment(g278,g276)
    c: Block(g276)
    c: Block(g270)
    c: Block(g264)
    c: Coincident(g279,g270)
    c: Coincident(g279,g264)
    c: Coincident(g280,g264)
    c: Coincident(g280,g276)
    c: Vertical(g280)
    c: Coincident(g281,g276)
    c: Coincident(g281,g270)
    c: Horizontal(g281)
    c: Weight(g282) = 1
    c: Equal(g282,g283)
    c: InternalAlignment(g282,g284)
    c: InternalAlignment(g283,g284)
    c: InternalAlignment(g285,g284)
    c: InternalAlignment(g286,g284)
    c: Weight(g287) = 1
    c: InternalAlignment(g288,g290)
    c: InternalAlignment(g289,g290)
    c: InternalAlignment(g291,g290)
    c: InternalAlignment(g292,g290)
    c: Weight(g293) = 1
    c: Equal(g293,g294)
    c: Equal(g293,g295)
    c: InternalAlignment(g293,g296)
    c: InternalAlignment(g294,g296)
    c: InternalAlignment(g295,g296)
    c: InternalAlignment(g297,g296)
    c: InternalAlignment(g298,g296)
    c: Equal(g299,g300)
    c: Equal(g299,g301)
    c: InternalAlignment(g299,g302)
    c: InternalAlignment(g300,g302)
    c: InternalAlignment(g301,g302)
    c: InternalAlignment(g303,g302)
    c: InternalAlignment(g304,g302)
    c: Block(g290)
    c: Block(g296)
    c: Block(g302)
    c: Block(g284)
    c: Coincident(g305,g284)
    c: Coincident(g305,g290)
    c: Horizontal(g305)
    c: Coincident(g306,g290)
    c: Coincident(g306,g296)
    c: Vertical(g306)
    c: Coincident(g307,g296)
    c: Coincident(g307,g302)
    c: Horizontal(g307)
    c: Coincident(g308,g302)
    c: Coincident(g308,g284)
    c: Weight(g309) = 1
    c: Equal(g309,g310)
    c: Equal(g309,g311)
    c: InternalAlignment(g309,g312)
    c: InternalAlignment(g310,g312)
    c: InternalAlignment(g311,g312)
    c: InternalAlignment(g313,g312)
    c: InternalAlignment(g314,g312)
    c: Weight(g315) = 1
    c: Equal(g315,g316)
    c: Equal(g315,g317)
    c: InternalAlignment(g315,g318)
    c: InternalAlignment(g316,g318)
    c: InternalAlignment(g317,g318)
    c: InternalAlignment(g319,g318)
    c: InternalAlignment(g320,g318)
    c: Weight(g321) = 1
    c: Equal(g321,g322)
    c: Equal(g321,g323)
    c: InternalAlignment(g321,g324)
    c: InternalAlignment(g322,g324)
    c: InternalAlignment(g323,g324)
    c: InternalAlignment(g325,g324)
    c: InternalAlignment(g326,g324)
    c: Block(g324)
    c: Block(g318)
    c: Block(g312)
    c: Coincident(g327,g324)
    c: Coincident(g327,g318)
    c: Horizontal(g327)
    c: Coincident(g328,g318)
    c: Coincident(g328,g312)
    c: Vertical(g328)
    c: Coincident(g329,g312)
    c: Coincident(g329,g324)
    c: InternalAlignment(g330,g331)
    c: InternalAlignment(g332,g331)
    c: InternalAlignment(g333,g331)
    c: Block(g331)
    c: Equal(g334,g335)
    c: Equal(g334,g336)
    c: InternalAlignment(g334,g337)
    c: InternalAlignment(g335,g337)
    c: InternalAlignment(g336,g337)
    c: InternalAlignment(g338,g337)
    c: InternalAlignment(g339,g337)
    c: Block(g337)
    c: Coincident(g340,g331)
    c: Horizontal(g340)
    c: Block(g340)
    c: Coincident(g341,g331)
    c: Coincident(g341,g257)
    c: Vertical(g341)
    c: Coincident(g342,g337)
    c: Coincident(g342,g251)
    c: Vertical(g342)
    c: Block(g343)
    c: Block(g5)
    c: Distance(g341) = 119.89
    c: Coincident(g344,g343)
    c: Coincident(g344,g5)
    c: Coincident(g345,g5)
    c: Coincident(g345,g343)
    c: Block(g6)
    c: Block(g346)
    c: Coincident(g347,g346)
    c: Coincident(g347,g6)
    c: Coincident(g348,g346)
    c: Coincident(g348,g6)
    c: Block(g348)
    c: Block(g347)
